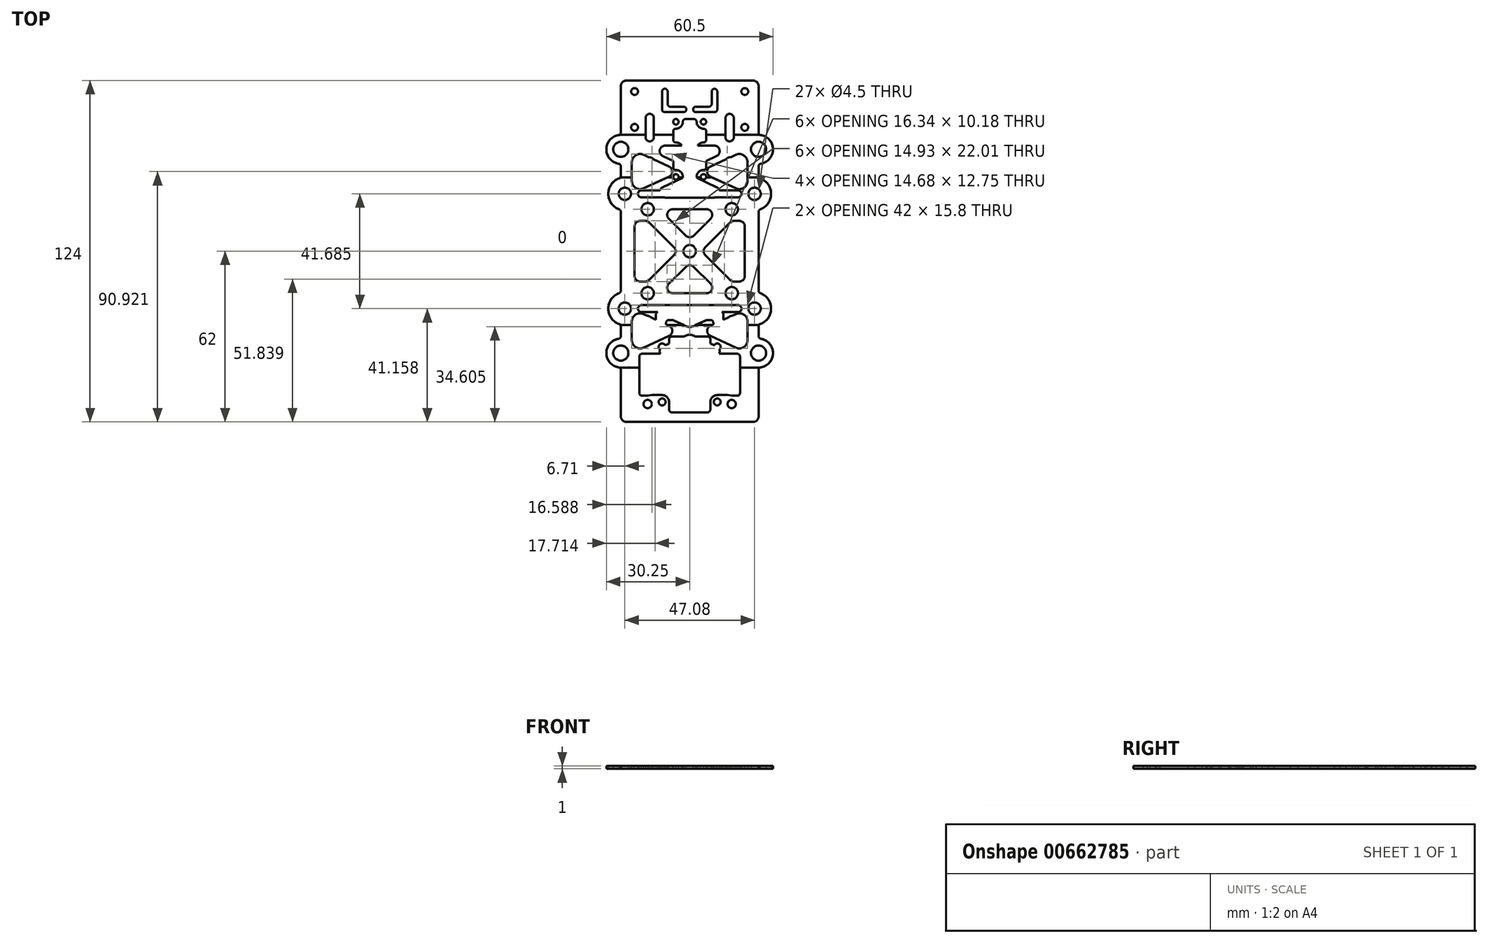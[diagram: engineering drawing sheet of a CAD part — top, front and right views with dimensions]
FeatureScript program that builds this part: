
annotation { "Feature Type Name" : "Feature", "Feature Type Description" : "" }
export const myFeature = defineFeature(function(context is Context, id is Id, definition is map)
    precondition{}
    {
        {
            var Q0;
            Q0=qCreatedBy(makeId("Top.planeOp"),FACE);
            var sketch = newSketch(context, id + "F0", { "sketchPlane" : qUnion([Q0])});
            skLineSegment(sketch, "E0.bottom", {"start": v(15.25, 15.25) * mm, "end": v(-15.25, 15.25) * mm, "construction": true});
            skLineSegment(sketch, "E0.top", {"start": v(15.25, -15.25) * mm, "end": v(-15.25, -15.25) * mm, "construction": true});
            skLineSegment(sketch, "E0.left", {"start": v(15.25, 15.25) * mm, "end": v(15.25, -15.25) * mm, "construction": true});
            skLineSegment(sketch, "E0.right", {"start": v(-15.25, 15.25) * mm, "end": v(-15.25, -15.25) * mm, "construction": true});
            skPoint(sketch, "E0.middle", {"position": v(0, 0) * mm});
            skLineSegment(sketch, "E1", {"start": v(15.25, 15.25) * mm, "end": v(23.54, 20.84) * mm});
            skLineSegment(sketch, "E2", {"start": v(23.54, 20.84) * mm, "end": v(92.7, 67.5) * mm});
            skCircle(sketch, "E3", {"center": v(92.7, 67.5) * mm, "radius": 63.5 * mm, "construction": true});
            skLineSegment(sketch, "E4", {"start": v(0, 0) * mm, "end": v(92.7, 0) * mm, "construction": true});
            skLineSegment(sketch, "E5.bottom", {"start": v(-25, 37) * mm, "end": v(25, 37) * mm, "construction": true});
            skLineSegment(sketch, "E5.top", {"start": v(-25, -37) * mm, "end": v(25, -37) * mm, "construction": true});
            skLineSegment(sketch, "E5.left", {"start": v(-25, 37) * mm, "end": v(-25, -37) * mm, "construction": true});
            skLineSegment(sketch, "E5.right", {"start": v(25, 37) * mm, "end": v(25, -37) * mm, "construction": true});
            skCircle(sketch, "E6", {"center": v(25, 37) * mm, "radius": 4.25 * mm, "construction": true});
            skCircle(sketch, "E7", {"center": v(15.25, 15.25) * mm, "radius": 1.5 * mm, "construction": true});
            skCircle(sketch, "E8", {"center": v(23.54, 20.84) * mm, "radius": 1.5 * mm, "construction": true});
            skCircle(sketch, "E9", {"center": v(92.7, 67.5) * mm, "radius": 50.8 * mm, "construction": true});
            skLineSegment(sketch, "E10.bottom", {"start": v(11.34, 21.05) * mm, "end": v(88.79, 73.3) * mm, "construction": true});
            skLineSegment(sketch, "E10.top", {"start": v(19.16, 9.45) * mm, "end": v(96.62, 61.7) * mm, "construction": true});
            skLineSegment(sketch, "E10.left", {"start": v(11.34, 21.05) * mm, "end": v(19.16, 9.45) * mm, "construction": true});
            skLineSegment(sketch, "E10.right", {"start": v(88.79, 73.3) * mm, "end": v(96.62, 61.7) * mm, "construction": true});
            skCircle(sketch, "E11", {"center": v(-25, 37) * mm, "radius": 4.25 * mm, "construction": true});
            skCircle(sketch, "E12", {"center": v(-25, -37) * mm, "radius": 4.25 * mm, "construction": true});
            skCircle(sketch, "E13", {"center": v(25, -37) * mm, "radius": 4.25 * mm, "construction": true});
            skCircle(sketch, "E14", {"center": v(-15.25, 15.25) * mm, "radius": 1.5 * mm, "construction": true});
            skCircle(sketch, "E15", {"center": v(-15.25, -15.25) * mm, "radius": 1.5 * mm, "construction": true});
            skCircle(sketch, "E16", {"center": v(15.25, -15.25) * mm, "radius": 1.5 * mm, "construction": true});
            skCircle(sketch, "E17.MirrorC", {"center": v(-23.54, 20.84) * mm, "radius": 1.5 * mm, "construction": true});
            skCircle(sketch, "E18.MirrorC", {"center": v(-23.54, -20.84) * mm, "radius": 1.5 * mm, "construction": true});
            skCircle(sketch, "E19.MirrorC", {"center": v(23.54, -20.84) * mm, "radius": 1.5 * mm, "construction": true});
            skSolve(sketch);
        }
        {
            var Q0;
            Q0=qCreatedBy(makeId("Top.planeOp"),FACE);
            var sketch = newSketch(context, id + "F1", { "sketchPlane" : qUnion([Q0])});
            skPoint(sketch, "E20.0", {"position": v(-25, 37) * mm});
            skPoint(sketch, "E21.0", {"position": v(25, 37) * mm});
            skPoint(sketch, "E22.0", {"position": v(25, -37) * mm});
            skPoint(sketch, "E23.0", {"position": v(-25, -37) * mm});
            skCircle(sketch, "E24.0", {"center": v(-23.54, -20.84) * mm, "radius": 1.5 * mm});
            skCircle(sketch, "E25.0", {"center": v(-15.25, -15.25) * mm, "radius": 1.5 * mm});
            skCircle(sketch, "E26.0", {"center": v(15.25, -15.25) * mm, "radius": 1.5 * mm});
            skCircle(sketch, "E27.0", {"center": v(23.54, -20.84) * mm, "radius": 1.5 * mm});
            skCircle(sketch, "E28.0", {"center": v(15.25, 15.25) * mm, "radius": 1.5 * mm});
            skCircle(sketch, "E29.0", {"center": v(-15.25, 15.25) * mm, "radius": 1.5 * mm});
            skCircle(sketch, "E30.0", {"center": v(-23.54, 20.84) * mm, "radius": 1.5 * mm});
            skCircle(sketch, "E31.0", {"center": v(23.54, 20.84) * mm, "radius": 1.5 * mm});
            skCircle(sketch, "E32", {"center": v(25, 37) * mm, "radius": 2.75 * mm});
            skCircle(sketch, "E33", {"center": v(-25, 37) * mm, "radius": 2.75 * mm});
            skCircle(sketch, "E34", {"center": v(-25, -37) * mm, "radius": 2.75 * mm});
            skCircle(sketch, "E35", {"center": v(25, -37) * mm, "radius": 2.75 * mm});
            skSolve(sketch);
        }
        {
            var Q0;
            Q0=qCreatedBy(makeId("Top.planeOp"),FACE);
            var sketch = newSketch(context, id + "F2", { "sketchPlane" : qUnion([Q0])});
            skCircle(sketch, "E36.0", {"center": v(-25, -37) * mm, "radius": 2.75 * mm});
            skCircle(sketch, "E37.0", {"center": v(-23.54, -20.84) * mm, "radius": 1.5 * mm});
            skCircle(sketch, "E38.0", {"center": v(-15.25, -15.25) * mm, "radius": 1.5 * mm});
            skCircle(sketch, "E39.0", {"center": v(15.25, -15.25) * mm, "radius": 1.5 * mm});
            skCircle(sketch, "E40.0", {"center": v(23.54, -20.84) * mm, "radius": 1.5 * mm});
            skCircle(sketch, "E41.0", {"center": v(-25, 37) * mm, "radius": 2.75 * mm});
            skCircle(sketch, "E42.0", {"center": v(-23.54, 20.84) * mm, "radius": 1.5 * mm});
            skCircle(sketch, "E43.0", {"center": v(-15.25, 15.25) * mm, "radius": 1.5 * mm});
            skCircle(sketch, "E44.0", {"center": v(15.25, 15.25) * mm, "radius": 1.5 * mm});
            skCircle(sketch, "E45.0", {"center": v(23.54, 20.84) * mm, "radius": 1.5 * mm});
            skCircle(sketch, "E46.0", {"center": v(25, 37) * mm, "radius": 2.75 * mm});
            skLineSegment(sketch, "E47.bottom", {"start": v(25, 62) * mm, "end": v(-25, 62) * mm});
            skLineSegment(sketch, "E47.top", {"start": v(25, -62) * mm, "end": v(-25, -62) * mm});
            skLineSegment(sketch, "E47.left", {"start": v(25, 62) * mm, "end": v(25, 42.25) * mm});
            skLineSegment(sketch, "E47.right", {"start": v(-25, 62) * mm, "end": v(-25, 42.25) * mm});
            skPoint(sketch, "E47.middle", {"position": v(0, 0) * mm});
            skArc(sketch, "E48", {"start": v(-25, 42.25) * mm, "mid": v(-30.25, 37) * mm, "end": v(-25, 31.75) * mm});
            skArc(sketch, "E49", {"start": v(-25, 26.66) * mm, "mid": v(-29.54, 20.84) * mm, "end": v(-25, 15.02) * mm});
            skArc(sketch, "E50", {"start": v(-25, -15.02) * mm, "mid": v(-29.54, -20.84) * mm, "end": v(-25, -26.66) * mm});
            skArc(sketch, "E51.MirrorCS", {"start": v(25, 42.25) * mm, "mid": v(30.25, 37) * mm, "end": v(25, 31.75) * mm});
            skArc(sketch, "E52.MirrorCS", {"start": v(25, 26.66) * mm, "mid": v(29.54, 20.84) * mm, "end": v(25, 15.02) * mm});
            skArc(sketch, "E53.MirrorCS", {"start": v(25, -15.02) * mm, "mid": v(29.54, -20.84) * mm, "end": v(25, -26.66) * mm});
            skArc(sketch, "E54", {"start": v(-25, -31.75) * mm, "mid": v(-30.25, -37) * mm, "end": v(-25, -42.25) * mm});
            skArc(sketch, "E55.MirrorCS", {"start": v(25, -31.75) * mm, "mid": v(30.25, -37) * mm, "end": v(25, -42.25) * mm});
            skLineSegment(sketch, "E56", {"start": v(-25, 42.25) * mm, "end": v(-25, 39.75) * mm, "construction": true});
            skLineSegment(sketch, "E57", {"start": v(-25, 31.75) * mm, "end": v(-25, 26.66) * mm});
            skLineSegment(sketch, "E58", {"start": v(-25, 34.25) * mm, "end": v(-25, 31.75) * mm, "construction": true});
            skLineSegment(sketch, "E59", {"start": v(-25, 39.75) * mm, "end": v(-25, 34.25) * mm, "construction": true});
            skLineSegment(sketch, "E60", {"start": v(25, 39.75) * mm, "end": v(25, 34.25) * mm, "construction": true});
            skLineSegment(sketch, "E61", {"start": v(25, 42.25) * mm, "end": v(25, 39.75) * mm, "construction": true});
            skLineSegment(sketch, "E62", {"start": v(25, 34.25) * mm, "end": v(25, 31.75) * mm, "construction": true});
            skLineSegment(sketch, "E63", {"start": v(25, 31.75) * mm, "end": v(25, 26.66) * mm});
            skLineSegment(sketch, "E64", {"start": v(-25, 26.66) * mm, "end": v(-25, 15.02) * mm, "construction": true});
            skLineSegment(sketch, "E65", {"start": v(-25, 15.02) * mm, "end": v(-25, -15.02) * mm});
            skLineSegment(sketch, "E66", {"start": v(25, 26.66) * mm, "end": v(25, 15.02) * mm, "construction": true});
            skLineSegment(sketch, "E67", {"start": v(25, 15.02) * mm, "end": v(25, -15.02) * mm});
            skLineSegment(sketch, "E68", {"start": v(-25, -31.75) * mm, "end": v(-25, -34.25) * mm, "construction": true});
            skLineSegment(sketch, "E69", {"start": v(-25, -42.25) * mm, "end": v(-25, -62) * mm});
            skLineSegment(sketch, "E70", {"start": v(-25, -39.75) * mm, "end": v(-25, -42.25) * mm, "construction": true});
            skLineSegment(sketch, "E71", {"start": v(-25, -34.25) * mm, "end": v(-25, -39.75) * mm, "construction": true});
            skLineSegment(sketch, "E72", {"start": v(-25, -26.66) * mm, "end": v(-25, -31.75) * mm});
            skLineSegment(sketch, "E73", {"start": v(-25, -15.02) * mm, "end": v(-25, -26.66) * mm, "construction": true});
            skLineSegment(sketch, "E74", {"start": v(25, -15.02) * mm, "end": v(25, -26.66) * mm});
            skLineSegment(sketch, "E75", {"start": v(25, -26.66) * mm, "end": v(25, -31.75) * mm});
            skLineSegment(sketch, "E76", {"start": v(25, -31.75) * mm, "end": v(25, -42.25) * mm, "construction": true});
            skLineSegment(sketch, "E77", {"start": v(25, -42.25) * mm, "end": v(25, -42.25) * mm});
            skArc(sketch, "E78", {"start": v(25, -34.25) * mm, "mid": v(22.25, -37) * mm, "end": v(25, -39.75) * mm});
            skArc(sketch, "E79", {"start": v(25, -39.75) * mm, "mid": v(27.75, -37) * mm, "end": v(25, -34.25) * mm});
            skLineSegment(sketch, "E80", {"start": v(25, -42.25) * mm, "end": v(25, -62) * mm});
            skSolve(sketch);
        }
        {
            var Q0;
            Q0=qSketchRegion(id+"F2",true);
            extrude(context, id + "F3", {"entities" : qUnion([Q0]), "depth" : 1 * mm, "offsetDistance" : 25 * mm});
        }
        {
            var Q0;
            Q0=qCreatedBy(makeId("Top.planeOp"),FACE);
            var sketch = newSketch(context, id + "F4", { "sketchPlane" : qUnion([Q0])});
            skCircle(sketch, "E81.0", {"center": v(-23.54, 20.84) * mm, "radius": 1.5 * mm});
            skCircle(sketch, "E82.0", {"center": v(-15.25, 15.25) * mm, "radius": 1.5 * mm});
            skCircle(sketch, "E83.0", {"center": v(15.25, 15.25) * mm, "radius": 1.5 * mm});
            skCircle(sketch, "E84.0", {"center": v(23.54, 20.84) * mm, "radius": 1.5 * mm});
            skCircle(sketch, "E85.0", {"center": v(-15.25, -15.25) * mm, "radius": 1.5 * mm});
            skCircle(sketch, "E86.0", {"center": v(-23.54, -20.84) * mm, "radius": 1.5 * mm});
            skCircle(sketch, "E87.0", {"center": v(15.25, -15.25) * mm, "radius": 1.5 * mm});
            skCircle(sketch, "E88.0", {"center": v(23.54, -20.84) * mm, "radius": 1.5 * mm});
            skArc(sketch, "E89.0", {"start": v(-25, 26.66) * mm, "mid": v(-29.54, 20.84) * mm, "end": v(-25, 15.02) * mm});
            skLineSegment(sketch, "E90.0", {"start": v(-25, 15.02) * mm, "end": v(-25, -15.02) * mm});
            skArc(sketch, "E91.0", {"start": v(-25, -15.02) * mm, "mid": v(-29.54, -20.84) * mm, "end": v(-25, -26.66) * mm});
            skLineSegment(sketch, "E92.0", {"start": v(25, 15.02) * mm, "end": v(25, -15.02) * mm});
            skArc(sketch, "E93.0", {"start": v(25, 26.66) * mm, "mid": v(29.54, 20.84) * mm, "end": v(25, 15.02) * mm});
            skArc(sketch, "E94.0", {"start": v(25, -15.02) * mm, "mid": v(29.54, -20.84) * mm, "end": v(25, -26.66) * mm});
            skArc(sketch, "E95", {"start": v(-25, 26.66) * mm, "mid": v(-24.28, 26.8) * mm, "end": v(-23.54, 26.84) * mm});
            skArc(sketch, "E96", {"start": v(-25, -26.66) * mm, "mid": v(-24.28, -26.8) * mm, "end": v(-23.54, -26.84) * mm});
            skArc(sketch, "E97", {"start": v(25, 26.66) * mm, "mid": v(24.28, 26.8) * mm, "end": v(23.54, 26.84) * mm});
            skArc(sketch, "E98", {"start": v(25, -26.66) * mm, "mid": v(24.28, -26.8) * mm, "end": v(23.54, -26.84) * mm});
            skLineSegment(sketch, "E99", {"start": v(-23.54, 26.84) * mm, "end": v(23.54, 26.84) * mm});
            skLineSegment(sketch, "E100", {"start": v(-23.54, -26.84) * mm, "end": v(23.54, -26.84) * mm});
            skSolve(sketch);
        }
        {
            var Q0;
            Q0=qCreatedBy(makeId("Top.planeOp"),FACE);
            var sketch = newSketch(context, id + "F5", { "sketchPlane" : qUnion([Q0])});
            skArc(sketch, "E101.0.0", {"start": v(25, -26.66) * mm, "mid": v(29.54, -20.84) * mm, "end": v(25, -15.02) * mm});
            skLineSegment(sketch, "E101.0.1", {"start": v(25, -15.02) * mm, "end": v(25, 15.02) * mm});
            skArc(sketch, "E101.0.2", {"start": v(25, 15.02) * mm, "mid": v(29.54, 20.84) * mm, "end": v(25, 26.66) * mm});
            skLineSegment(sketch, "E101.0.3", {"start": v(25, 26.66) * mm, "end": v(25, 31.75) * mm});
            skArc(sketch, "E101.0.4", {"start": v(25, 31.75) * mm, "mid": v(30.25, 37) * mm, "end": v(25, 42.25) * mm});
            skLineSegment(sketch, "E101.0.5", {"start": v(25, 42.25) * mm, "end": v(25, 62) * mm});
            skLineSegment(sketch, "E101.0.6", {"start": v(25, 62) * mm, "end": v(-25, 62) * mm, "construction": true});
            skLineSegment(sketch, "E101.0.7", {"start": v(-25, 62) * mm, "end": v(-25, 42.25) * mm});
            skArc(sketch, "E101.0.8", {"start": v(-25, 42.25) * mm, "mid": v(-30.25, 37) * mm, "end": v(-25, 31.75) * mm});
            skLineSegment(sketch, "E101.0.9", {"start": v(-25, 31.75) * mm, "end": v(-25, 26.66) * mm});
            skArc(sketch, "E101.0.10", {"start": v(-25, 26.66) * mm, "mid": v(-29.54, 20.84) * mm, "end": v(-25, 15.02) * mm});
            skLineSegment(sketch, "E101.0.11", {"start": v(-25, 15.02) * mm, "end": v(-25, -15.02) * mm});
            skArc(sketch, "E101.0.12", {"start": v(-25, -15.02) * mm, "mid": v(-29.54, -20.84) * mm, "end": v(-25, -26.66) * mm});
            skLineSegment(sketch, "E101.0.13", {"start": v(-25, -26.66) * mm, "end": v(-25, -31.75) * mm});
            skArc(sketch, "E101.0.14", {"start": v(-25, -31.75) * mm, "mid": v(-30.25, -37) * mm, "end": v(-25, -42.25) * mm});
            skLineSegment(sketch, "E101.0.15", {"start": v(-25, -42.25) * mm, "end": v(-25, -62) * mm});
            skLineSegment(sketch, "E101.0.16", {"start": v(-25, -62) * mm, "end": v(25, -62) * mm, "construction": true});
            skLineSegment(sketch, "E101.0.17", {"start": v(25, -62) * mm, "end": v(25, -42.25) * mm});
            skArc(sketch, "E101.0.18", {"start": v(25, -42.25) * mm, "mid": v(30.25, -37) * mm, "end": v(25, -31.75) * mm});
            skLineSegment(sketch, "E101.0.19", {"start": v(25, -31.75) * mm, "end": v(25, -26.66) * mm});
            skLineSegment(sketch, "E102", {"start": v(-25, 42.25) * mm, "end": v(25, 42.25) * mm});
            skLineSegment(sketch, "E103", {"start": v(-25, -42.25) * mm, "end": v(25, -42.25) * mm});
            skCircle(sketch, "E104.0", {"center": v(-25, 37) * mm, "radius": 2.75 * mm});
            skCircle(sketch, "E105.0", {"center": v(-23.54, 20.84) * mm, "radius": 1.5 * mm});
            skCircle(sketch, "E106.0", {"center": v(-15.25, 15.25) * mm, "radius": 1.5 * mm});
            skCircle(sketch, "E107.0", {"center": v(15.25, 15.25) * mm, "radius": 1.5 * mm});
            skCircle(sketch, "E108.0", {"center": v(23.54, 20.84) * mm, "radius": 1.5 * mm});
            skCircle(sketch, "E109.0", {"center": v(25, 37) * mm, "radius": 2.75 * mm});
            skCircle(sketch, "E110.0", {"center": v(-23.54, -20.84) * mm, "radius": 1.5 * mm});
            skCircle(sketch, "E111.0", {"center": v(-15.25, -15.25) * mm, "radius": 1.5 * mm});
            skCircle(sketch, "E112.0", {"center": v(15.25, -15.25) * mm, "radius": 1.5 * mm});
            skCircle(sketch, "E113.0", {"center": v(23.54, -20.84) * mm, "radius": 1.5 * mm});
            skCircle(sketch, "E114.0", {"center": v(-25, -37) * mm, "radius": 2.75 * mm});
            skCircle(sketch, "E115.0", {"center": v(25, -37) * mm, "radius": 2.75 * mm});
            skSolve(sketch);
        }
        {
            var Q0;
            Q0=qSketchRegion(id+"F4",true);
            extrude(context, id + "F6", {"entities" : qUnion([Q0]), "depth" : 1 * mm, "offsetDistance" : 25 * mm});
        }
        {
            var Q0;
            Q0=qSketchRegion(id+"F5",true);
            extrude(context, id + "F7", {"entities" : qUnion([Q0]), "depth" : 1 * mm, "offsetDistance" : 25 * mm});
        }
        {
            var Q0;
            Q0=makeQuery(id+"F3.opExtrude","SWEPT_EDGE",EDGE,{"disambiguationData":[OSD([sQuery(id+"F2.wireOp",EDGE,"E47.top"),sQuery(id+"F2.wireOp",EDGE,"E69")])]});
            var Q1;
            Q1=makeQuery(id+"F3.opExtrude","SWEPT_EDGE",EDGE,{"disambiguationData":[OSD([sQuery(id+"F2.wireOp",EDGE,"E47.top"),sQuery(id+"F2.wireOp",EDGE,"E80")])]});
            var Q2;
            Q2=makeQuery(id+"F3.opExtrude","SWEPT_EDGE",EDGE,{"disambiguationData":[OSD([sQuery(id+"F2.wireOp",EDGE,"E47.bottom"),sQuery(id+"F2.wireOp",EDGE,"E47.right")])]});
            var Q3;
            Q3=makeQuery(id+"F3.opExtrude","SWEPT_EDGE",EDGE,{"disambiguationData":[OSD([sQuery(id+"F2.wireOp",EDGE,"E47.bottom"),sQuery(id+"F2.wireOp",EDGE,"E47.left")])]});
            fillet(context, id + "F8", {"entities" : qUnion([Q0, Q1, Q2, Q3]), "radius" : 2 * mm, "allowEdgeOverflow" : false});
        }
        {
            var Q0;
            Q0=makeQuery(id+"F3.opExtrude","SWEPT_EDGE",EDGE,{"disambiguationData":[OSD([sQuery(id+"F2.wireOp",EDGE,"E47.left"),sQuery(id+"F2.wireOp",EDGE,"E51.MirrorCS")])]});
            var Q1;
            Q1=makeQuery(id+"F3.opExtrude","SWEPT_EDGE",EDGE,{"disambiguationData":[OSD([sQuery(id+"F2.wireOp",EDGE,"E51.MirrorCS"),sQuery(id+"F2.wireOp",EDGE,"E63")])]});
            var Q2;
            Q2=makeQuery(id+"F3.opExtrude","SWEPT_EDGE",EDGE,{"disambiguationData":[OSD([sQuery(id+"F2.wireOp",EDGE,"E52.MirrorCS"),sQuery(id+"F2.wireOp",EDGE,"E63")])]});
            var Q3;
            Q3=makeQuery(id+"F3.opExtrude","SWEPT_EDGE",EDGE,{"disambiguationData":[OSD([sQuery(id+"F2.wireOp",EDGE,"E52.MirrorCS"),sQuery(id+"F2.wireOp",EDGE,"E67")])]});
            var Q4;
            Q4=makeQuery(id+"F3.opExtrude","SWEPT_EDGE",EDGE,{"disambiguationData":[OSD([sQuery(id+"F2.wireOp",EDGE,"E53.MirrorCS"),sQuery(id+"F2.wireOp",EDGE,"E67"),sQuery(id+"F2.wireOp",EDGE,"E74")])]});
            var Q5;
            Q5=makeQuery(id+"F3.opExtrude","SWEPT_EDGE",EDGE,{"disambiguationData":[OSD([sQuery(id+"F2.wireOp",EDGE,"E55.MirrorCS"),sQuery(id+"F2.wireOp",EDGE,"E75")])]});
            var Q6;
            Q6=makeQuery(id+"F3.opExtrude","SWEPT_EDGE",EDGE,{"disambiguationData":[OSD([sQuery(id+"F2.wireOp",EDGE,"E55.MirrorCS"),sQuery(id+"F2.wireOp",EDGE,"E80")])]});
            var Q7;
            Q7=makeQuery(id+"F3.opExtrude","SWEPT_EDGE",EDGE,{"disambiguationData":[OSD([sQuery(id+"F2.wireOp",EDGE,"E47.right"),sQuery(id+"F2.wireOp",EDGE,"E48")])]});
            var Q8;
            Q8=makeQuery(id+"F3.opExtrude","SWEPT_EDGE",EDGE,{"disambiguationData":[OSD([sQuery(id+"F2.wireOp",EDGE,"E49"),sQuery(id+"F2.wireOp",EDGE,"E57")])]});
            var Q9;
            Q9=makeQuery(id+"F3.opExtrude","SWEPT_EDGE",EDGE,{"disambiguationData":[OSD([sQuery(id+"F2.wireOp",EDGE,"E48"),sQuery(id+"F2.wireOp",EDGE,"E57")])]});
            var Q10;
            Q10=makeQuery(id+"F3.opExtrude","SWEPT_EDGE",EDGE,{"disambiguationData":[OSD([sQuery(id+"F2.wireOp",EDGE,"E49"),sQuery(id+"F2.wireOp",EDGE,"E65")])]});
            var Q11;
            Q11=makeQuery(id+"F3.opExtrude","SWEPT_EDGE",EDGE,{"disambiguationData":[OSD([sQuery(id+"F2.wireOp",EDGE,"E50"),sQuery(id+"F2.wireOp",EDGE,"E72")])]});
            var Q12;
            Q12=makeQuery(id+"F3.opExtrude","SWEPT_EDGE",EDGE,{"disambiguationData":[OSD([sQuery(id+"F2.wireOp",EDGE,"E50"),sQuery(id+"F2.wireOp",EDGE,"E65")])]});
            var Q13;
            Q13=makeQuery(id+"F3.opExtrude","SWEPT_EDGE",EDGE,{"disambiguationData":[OSD([sQuery(id+"F2.wireOp",EDGE,"E54"),sQuery(id+"F2.wireOp",EDGE,"E72")])]});
            var Q14;
            Q14=makeQuery(id+"F3.opExtrude","SWEPT_EDGE",EDGE,{"disambiguationData":[OSD([sQuery(id+"F2.wireOp",EDGE,"E54"),sQuery(id+"F2.wireOp",EDGE,"E69")])]});
            var Q15;
            Q15=makeQuery(id+"F7.opExtrude","SWEPT_EDGE",EDGE,{"disambiguationData":[OSD([sQuery(id+"F5.wireOp",EDGE,"E101.0.9"),sQuery(id+"F5.wireOp",EDGE,"E101.0.10")])]});
            var Q16;
            Q16=makeQuery(id+"F7.opExtrude","SWEPT_EDGE",EDGE,{"disambiguationData":[OSD([sQuery(id+"F5.wireOp",EDGE,"E101.0.8"),sQuery(id+"F5.wireOp",EDGE,"E101.0.9")])]});
            var Q17;
            Q17=makeQuery(id+"F7.opExtrude","SWEPT_EDGE",EDGE,{"disambiguationData":[OSD([sQuery(id+"F5.wireOp",EDGE,"E101.0.10"),sQuery(id+"F5.wireOp",EDGE,"E101.0.11")])]});
            var Q18;
            Q18=makeQuery(id+"F7.opExtrude","SWEPT_EDGE",EDGE,{"disambiguationData":[OSD([sQuery(id+"F5.wireOp",EDGE,"E101.0.11"),sQuery(id+"F5.wireOp",EDGE,"E101.0.12")])]});
            var Q19;
            Q19=makeQuery(id+"F7.opExtrude","SWEPT_EDGE",EDGE,{"disambiguationData":[OSD([sQuery(id+"F5.wireOp",EDGE,"E101.0.12"),sQuery(id+"F5.wireOp",EDGE,"E101.0.13")])]});
            var Q20;
            Q20=makeQuery(id+"F7.opExtrude","SWEPT_EDGE",EDGE,{"disambiguationData":[OSD([sQuery(id+"F5.wireOp",EDGE,"E101.0.13"),sQuery(id+"F5.wireOp",EDGE,"E101.0.14")])]});
            var Q21;
            Q21=makeQuery(id+"F7.opExtrude","SWEPT_EDGE",EDGE,{"disambiguationData":[OSD([sQuery(id+"F5.wireOp",EDGE,"E101.0.1"),sQuery(id+"F5.wireOp",EDGE,"E101.0.2")])]});
            var Q22;
            Q22=makeQuery(id+"F7.opExtrude","SWEPT_EDGE",EDGE,{"disambiguationData":[OSD([sQuery(id+"F5.wireOp",EDGE,"E101.0.2"),sQuery(id+"F5.wireOp",EDGE,"E101.0.3")])]});
            var Q23;
            Q23=makeQuery(id+"F7.opExtrude","SWEPT_EDGE",EDGE,{"disambiguationData":[OSD([sQuery(id+"F5.wireOp",EDGE,"E101.0.3"),sQuery(id+"F5.wireOp",EDGE,"E101.0.4")])]});
            var Q24;
            Q24=makeQuery(id+"F7.opExtrude","SWEPT_EDGE",EDGE,{"disambiguationData":[OSD([sQuery(id+"F5.wireOp",EDGE,"E101.0.18"),sQuery(id+"F5.wireOp",EDGE,"E101.0.19")])]});
            var Q25;
            Q25=makeQuery(id+"F7.opExtrude","SWEPT_EDGE",EDGE,{"disambiguationData":[OSD([sQuery(id+"F5.wireOp",EDGE,"E101.0.0"),sQuery(id+"F5.wireOp",EDGE,"E101.0.19")])]});
            var Q26;
            Q26=makeQuery(id+"F7.opExtrude","SWEPT_EDGE",EDGE,{"disambiguationData":[OSD([sQuery(id+"F5.wireOp",EDGE,"E101.0.0"),sQuery(id+"F5.wireOp",EDGE,"E101.0.1")])]});
            var Q27;
            Q27=makeQuery(id+"F3.opExtrude","SWEPT_EDGE",EDGE,{"disambiguationData":[OSD([sQuery(id+"F2.wireOp",EDGE,"E53.MirrorCS"),sQuery(id+"F2.wireOp",EDGE,"E74"),sQuery(id+"F2.wireOp",EDGE,"E75")])]});
            var Q28;
            Q28=makeQuery(id+"F6.opExtrude","SWEPT_EDGE",EDGE,{"disambiguationData":[OSD([sQuery(id+"F4.wireOp",EDGE,"E92.0"),sQuery(id+"F4.wireOp",EDGE,"E94.0")])]});
            var Q29;
            Q29=makeQuery(id+"F6.opExtrude","SWEPT_EDGE",EDGE,{"disambiguationData":[OSD([sQuery(id+"F4.wireOp",EDGE,"E92.0"),sQuery(id+"F4.wireOp",EDGE,"E93.0")])]});
            var Q30;
            Q30=makeQuery(id+"F6.opExtrude","SWEPT_EDGE",EDGE,{"disambiguationData":[OSD([sQuery(id+"F4.wireOp",EDGE,"E89.0"),sQuery(id+"F4.wireOp",EDGE,"E90.0")])]});
            var Q31;
            Q31=makeQuery(id+"F6.opExtrude","SWEPT_EDGE",EDGE,{"disambiguationData":[OSD([sQuery(id+"F4.wireOp",EDGE,"E90.0"),sQuery(id+"F4.wireOp",EDGE,"E91.0")])]});
            fillet(context, id + "F9", {"entities" : qUnion([Q0, Q1, Q2, Q3, Q4, Q5, Q6, Q7, Q8, Q9, Q10, Q11, Q12, Q13, Q14, Q15, Q16, Q17, Q18, Q19, Q20, Q21, Q22, Q23, Q24, Q25, Q26, Q27, Q28, Q29, Q30, Q31]), "radius" : 1 * mm, "allowEdgeOverflow" : false});
        }
        {
            var Q0;
            Q0=makeQuery(id+"F3.opExtrude","CAP_FACE",FACE,{"disambiguationData":[OSD([sQuery(id+"F2.wireOp",EDGE,"E36.0"),sQuery(id+"F2.wireOp",EDGE,"E37.0"),sQuery(id+"F2.wireOp",EDGE,"E38.0"),sQuery(id+"F2.wireOp",EDGE,"E39.0"),sQuery(id+"F2.wireOp",EDGE,"E40.0"),sQuery(id+"F2.wireOp",EDGE,"E41.0"),sQuery(id+"F2.wireOp",EDGE,"E42.0"),sQuery(id+"F2.wireOp",EDGE,"E43.0"),sQuery(id+"F2.wireOp",EDGE,"E44.0"),sQuery(id+"F2.wireOp",EDGE,"E45.0"),sQuery(id+"F2.wireOp",EDGE,"E46.0"),sQuery(id+"F2.wireOp",EDGE,"E47.bottom"),sQuery(id+"F2.wireOp",EDGE,"E47.top"),sQuery(id+"F2.wireOp",EDGE,"E47.left"),sQuery(id+"F2.wireOp",EDGE,"E47.right"),sQuery(id+"F2.wireOp",EDGE,"E48"),sQuery(id+"F2.wireOp",EDGE,"E49"),sQuery(id+"F2.wireOp",EDGE,"E50"),sQuery(id+"F2.wireOp",EDGE,"E51.MirrorCS"),sQuery(id+"F2.wireOp",EDGE,"E52.MirrorCS"),sQuery(id+"F2.wireOp",EDGE,"E53.MirrorCS"),sQuery(id+"F2.wireOp",EDGE,"E54"),sQuery(id+"F2.wireOp",EDGE,"E55.MirrorCS"),sQuery(id+"F2.wireOp",EDGE,"rjWOpLop-ofpK-hTEo-auwK-LkPdoEbubAMj"),sQuery(id+"F2.wireOp",EDGE,"E57"),sQuery(id+"F2.wireOp",EDGE,"E63"),sQuery(id+"F2.wireOp",EDGE,"E65"),sQuery(id+"F2.wireOp",EDGE,"E67"),sQuery(id+"F2.wireOp",EDGE,"E69"),sQuery(id+"F2.wireOp",EDGE,"E72"),sQuery(id+"F2.wireOp",EDGE,"E75"),sQuery(id+"F2.wireOp",EDGE,"E78"),sQuery(id+"F2.wireOp",EDGE,"E79"),sQuery(id+"F2.wireOp",EDGE,"E80")])],"isStart":false});
            var sketch = newSketch(context, id + "F10", { "sketchPlane" : qUnion([Q0])});
            skLineSegment(sketch, "E116.0.0", {"start": v(25, 43.17) * mm, "end": v(25, 60) * mm, "construction": true});
            skArc(sketch, "E116.0.1", {"start": v(25, 60) * mm, "mid": v(24.41, 61.41) * mm, "end": v(23, 62) * mm, "construction": true});
            skLineSegment(sketch, "E116.0.2", {"start": v(23, 62) * mm, "end": v(-23, 62) * mm, "construction": true});
            skArc(sketch, "E116.0.3", {"start": v(-23, 62) * mm, "mid": v(-24.41, 61.41) * mm, "end": v(-25, 60) * mm, "construction": true});
            skLineSegment(sketch, "E116.0.4", {"start": v(-25, 60) * mm, "end": v(-25, 43.17) * mm, "construction": true});
            skArc(sketch, "E116.0.5", {"start": v(-25, 43.17) * mm, "mid": v(-25.24, 42.52) * mm, "end": v(-25.84, 42.18) * mm, "construction": true});
            skArc(sketch, "E116.0.6", {"start": v(-25.84, 42.18) * mm, "mid": v(-30.25, 37) * mm, "end": v(-25.84, 31.82) * mm, "construction": true});
            skArc(sketch, "E116.0.7", {"start": v(-25.84, 31.82) * mm, "mid": v(-25.24, 31.48) * mm, "end": v(-25, 30.83) * mm, "construction": true});
            skLineSegment(sketch, "E116.0.8", {"start": v(-25, 30.83) * mm, "end": v(-25, 27.4) * mm, "construction": true});
            skArc(sketch, "E116.0.9", {"start": v(-25, 27.4) * mm, "mid": v(-25.18, 26.83) * mm, "end": v(-25.65, 26.46) * mm, "construction": true});
            skArc(sketch, "E116.0.10", {"start": v(-25.65, 26.46) * mm, "mid": v(-29.54, 20.84) * mm, "end": v(-25.65, 15.23) * mm, "construction": true});
            skArc(sketch, "E116.0.11", {"start": v(-25.65, 15.23) * mm, "mid": v(-25.18, 14.86) * mm, "end": v(-25, 14.29) * mm, "construction": true});
            skLineSegment(sketch, "E116.0.12", {"start": v(-25, 14.29) * mm, "end": v(-25, -14.29) * mm, "construction": true});
            skArc(sketch, "E116.0.13", {"start": v(-25, -14.29) * mm, "mid": v(-25.18, -14.86) * mm, "end": v(-25.65, -15.23) * mm, "construction": true});
            skArc(sketch, "E116.0.14", {"start": v(-25.65, -15.23) * mm, "mid": v(-29.54, -20.84) * mm, "end": v(-25.65, -26.46) * mm, "construction": true});
            skArc(sketch, "E116.0.15", {"start": v(-25.65, -26.46) * mm, "mid": v(-25.18, -26.83) * mm, "end": v(-25, -27.4) * mm, "construction": true});
            skLineSegment(sketch, "E116.0.16", {"start": v(-25, -27.4) * mm, "end": v(-25, -30.83) * mm, "construction": true});
            skArc(sketch, "E116.0.17", {"start": v(-25, -30.83) * mm, "mid": v(-25.24, -31.48) * mm, "end": v(-25.84, -31.82) * mm, "construction": true});
            skArc(sketch, "E116.0.18", {"start": v(-25.84, -31.82) * mm, "mid": v(-30.25, -37) * mm, "end": v(-25.84, -42.18) * mm, "construction": true});
            skArc(sketch, "E116.0.19", {"start": v(-25.84, -42.18) * mm, "mid": v(-25.24, -42.52) * mm, "end": v(-25, -43.17) * mm, "construction": true});
            skLineSegment(sketch, "E116.0.20", {"start": v(-25, -43.17) * mm, "end": v(-25, -60) * mm, "construction": true});
            skArc(sketch, "E116.0.21", {"start": v(-25, -60) * mm, "mid": v(-24.41, -61.41) * mm, "end": v(-23, -62) * mm, "construction": true});
            skLineSegment(sketch, "E116.0.22", {"start": v(-23, -62) * mm, "end": v(23, -62) * mm, "construction": true});
            skArc(sketch, "E116.0.23", {"start": v(23, -62) * mm, "mid": v(24.41, -61.41) * mm, "end": v(25, -60) * mm, "construction": true});
            skLineSegment(sketch, "E116.0.24", {"start": v(25, -60) * mm, "end": v(25, -43.17) * mm, "construction": true});
            skArc(sketch, "E116.0.25", {"start": v(25, -43.17) * mm, "mid": v(25.24, -42.52) * mm, "end": v(25.84, -42.18) * mm, "construction": true});
            skArc(sketch, "E116.0.26", {"start": v(25.84, -42.18) * mm, "mid": v(30.25, -37) * mm, "end": v(25.84, -31.82) * mm, "construction": true});
            skArc(sketch, "E116.0.27", {"start": v(25.84, -31.82) * mm, "mid": v(25.24, -31.48) * mm, "end": v(25, -30.83) * mm, "construction": true});
            skLineSegment(sketch, "E116.0.28", {"start": v(25, -30.83) * mm, "end": v(25, -27.4) * mm, "construction": true});
            skArc(sketch, "E116.0.29", {"start": v(25, -27.4) * mm, "mid": v(25.18, -26.83) * mm, "end": v(25.65, -26.46) * mm, "construction": true});
            skArc(sketch, "E116.0.30", {"start": v(25.65, -26.46) * mm, "mid": v(29.54, -20.84) * mm, "end": v(25.65, -15.23) * mm, "construction": true});
            skArc(sketch, "E116.0.31", {"start": v(25.65, -15.23) * mm, "mid": v(25.18, -14.86) * mm, "end": v(25, -14.29) * mm, "construction": true});
            skLineSegment(sketch, "E116.0.32", {"start": v(25, -14.29) * mm, "end": v(25, 14.29) * mm, "construction": true});
            skArc(sketch, "E116.0.33", {"start": v(25, 14.29) * mm, "mid": v(25.18, 14.86) * mm, "end": v(25.65, 15.23) * mm, "construction": true});
            skArc(sketch, "E116.0.34", {"start": v(25.65, 15.23) * mm, "mid": v(29.54, 20.84) * mm, "end": v(25.65, 26.46) * mm, "construction": true});
            skArc(sketch, "E116.0.35", {"start": v(25.65, 26.46) * mm, "mid": v(25.18, 26.83) * mm, "end": v(25, 27.4) * mm, "construction": true});
            skLineSegment(sketch, "E116.0.36", {"start": v(25, 27.4) * mm, "end": v(25, 30.83) * mm, "construction": true});
            skArc(sketch, "E116.0.37", {"start": v(25, 30.83) * mm, "mid": v(25.24, 31.48) * mm, "end": v(25.84, 31.82) * mm, "construction": true});
            skArc(sketch, "E116.0.38", {"start": v(25.84, 31.82) * mm, "mid": v(30.25, 37) * mm, "end": v(25.84, 42.18) * mm, "construction": true});
            skArc(sketch, "E116.0.39", {"start": v(25.84, 42.18) * mm, "mid": v(25.24, 42.52) * mm, "end": v(25, 43.17) * mm, "construction": true});
            skCircle(sketch, "E117", {"center": v(-23.54, -20.84) * mm, "radius": 2.25 * mm});
            skCircle(sketch, "E118", {"center": v(-15.25, -15.25) * mm, "radius": 2.25 * mm});
            skCircle(sketch, "E119", {"center": v(15.25, -15.25) * mm, "radius": 2.25 * mm});
            skCircle(sketch, "E120", {"center": v(23.54, -20.84) * mm, "radius": 2.25 * mm});
            skCircle(sketch, "E121", {"center": v(-15.25, 15.25) * mm, "radius": 2.25 * mm});
            skCircle(sketch, "E122", {"center": v(-23.54, 20.84) * mm, "radius": 2.25 * mm});
            skCircle(sketch, "E123", {"center": v(15.25, 15.25) * mm, "radius": 2.25 * mm});
            skCircle(sketch, "E124", {"center": v(23.54, 20.84) * mm, "radius": 2.25 * mm});
            skLineSegment(sketch, "E125.bottom", {"start": v(10, -34.75) * mm, "end": v(-10, -34.75) * mm, "construction": true});
            skLineSegment(sketch, "E125.top", {"start": v(10, -54.75) * mm, "end": v(-10, -54.75) * mm, "construction": true});
            skLineSegment(sketch, "E125.left", {"start": v(10, -34.75) * mm, "end": v(10, -54.75) * mm, "construction": true});
            skLineSegment(sketch, "E125.right", {"start": v(-10, -34.75) * mm, "end": v(-10, -54.75) * mm, "construction": true});
            skPoint(sketch, "E125.middle", {"position": v(0, -44.75) * mm});
            skCircle(sketch, "E126", {"center": v(-10, -34.75) * mm, "radius": 1.25 * mm});
            skCircle(sketch, "E127", {"center": v(10, -34.75) * mm, "radius": 1.25 * mm});
            skCircle(sketch, "E128", {"center": v(10, -54.75) * mm, "radius": 1.25 * mm});
            skCircle(sketch, "E129", {"center": v(-10, -54.75) * mm, "radius": 1.25 * mm});
            skLineSegment(sketch, "E130.bottom", {"start": v(15.25, -25) * mm, "end": v(-15.25, -25) * mm, "construction": true});
            skLineSegment(sketch, "E130.top", {"start": v(15.25, -55.5) * mm, "end": v(-15.25, -55.5) * mm, "construction": true});
            skLineSegment(sketch, "E130.left", {"start": v(15.25, -25) * mm, "end": v(15.25, -55.5) * mm, "construction": true});
            skLineSegment(sketch, "E130.right", {"start": v(-15.25, -25) * mm, "end": v(-15.25, -55.5) * mm, "construction": true});
            skPoint(sketch, "E130.middle", {"position": v(0, -40.25) * mm});
            skCircle(sketch, "E131", {"center": v(15.25, -25) * mm, "radius": 1.5 * mm});
            skCircle(sketch, "E132", {"center": v(-15.25, -25) * mm, "radius": 1.5 * mm});
            skCircle(sketch, "E133", {"center": v(-15.25, -55.5) * mm, "radius": 1.5 * mm});
            skCircle(sketch, "E134", {"center": v(15.25, -55.5) * mm, "radius": 1.5 * mm});
            skLineSegment(sketch, "E135.bottom", {"start": v(18, -22.25) * mm, "end": v(-18, -22.25) * mm, "construction": true});
            skLineSegment(sketch, "E135.top", {"start": v(18, -58.25) * mm, "end": v(-18, -58.25) * mm, "construction": true});
            skLineSegment(sketch, "E135.left", {"start": v(18, -22.25) * mm, "end": v(18, -58.25) * mm, "construction": true});
            skLineSegment(sketch, "E135.right", {"start": v(-18, -22.25) * mm, "end": v(-18, -58.25) * mm, "construction": true});
            skLineSegment(sketch, "E136.bottom", {"start": v(13.5, -31.25) * mm, "end": v(-13.5, -31.25) * mm, "construction": true});
            skLineSegment(sketch, "E136.top", {"start": v(13.5, -58.25) * mm, "end": v(-13.5, -58.25) * mm, "construction": true});
            skLineSegment(sketch, "E136.left", {"start": v(13.5, -31.25) * mm, "end": v(13.5, -58.25) * mm, "construction": true});
            skLineSegment(sketch, "E136.right", {"start": v(-13.5, -31.25) * mm, "end": v(-13.5, -55.5) * mm, "construction": true});
            skArc(sketch, "E137", {"start": v(-10, -52.25) * mm, "mid": v(-8.23, -52.98) * mm, "end": v(-7.5, -54.75) * mm});
            skArc(sketch, "E138", {"start": v(-10, -37.25) * mm, "mid": v(-8.23, -36.52) * mm, "end": v(-7.5, -34.75) * mm});
            skArc(sketch, "E139", {"start": v(7.5, -34.75) * mm, "mid": v(8.23, -36.52) * mm, "end": v(10, -37.25) * mm});
            skArc(sketch, "E140", {"start": v(10, -52.25) * mm, "mid": v(8.23, -52.98) * mm, "end": v(7.5, -54.75) * mm});
            skLineSegment(sketch, "E141.0", {"start": v(18.25, -22) * mm, "end": v(-18.25, -22) * mm, "construction": true});
            skLineSegment(sketch, "E141.1", {"start": v(18.25, -22) * mm, "end": v(18.25, -58.5) * mm, "construction": true});
            skLineSegment(sketch, "E141.2", {"start": v(18.25, -58.5) * mm, "end": v(-18.25, -58.5) * mm, "construction": true});
            skLineSegment(sketch, "E141.3", {"start": v(-18.25, -22) * mm, "end": v(-18.25, -58.5) * mm, "construction": true});
            skLineSegment(sketch, "E142", {"start": v(-7.5, -54.75) * mm, "end": v(-7.5, -58.5) * mm});
            skLineSegment(sketch, "E143", {"start": v(7.5, -54.75) * mm, "end": v(7.5, -58.5) * mm});
            skLineSegment(sketch, "E144", {"start": v(-7.5, -58.5) * mm, "end": v(7.5, -58.5) * mm});
            skLineSegment(sketch, "E145.0", {"start": v(-13.75, -31) * mm, "end": v(-13.75, -58.5) * mm, "construction": true});
            skLineSegment(sketch, "E145.1", {"start": v(13.75, -31) * mm, "end": v(-13.75, -31) * mm, "construction": true});
            skLineSegment(sketch, "E145.2", {"start": v(13.75, -31) * mm, "end": v(13.75, -58.5) * mm, "construction": true});
            skLineSegment(sketch, "E146", {"start": v(-7.5, -34.75) * mm, "end": v(-7.5, -31) * mm});
            skLineSegment(sketch, "E147", {"start": v(7.5, -34.75) * mm, "end": v(7.5, -31) * mm});
            skLineSegment(sketch, "E148", {"start": v(-18.25, -37.25) * mm, "end": v(-18.25, -52.5) * mm});
            skLineSegment(sketch, "E149", {"start": v(18.25, -37.25) * mm, "end": v(18.25, -52.5) * mm});
            skArc(sketch, "E150", {"start": v(-15.25, -28) * mm, "mid": v(-13.13, -27.12) * mm, "end": v(-12.25, -25) * mm});
            skArc(sketch, "E151", {"start": v(12.25, -25) * mm, "mid": v(13.13, -27.12) * mm, "end": v(15.25, -28) * mm});
            skLineSegment(sketch, "E152", {"start": v(-12.25, -25) * mm, "end": v(-12.25, -22) * mm});
            skLineSegment(sketch, "E153", {"start": v(-15.25, -28) * mm, "end": v(-18.25, -28) * mm});
            skLineSegment(sketch, "E154", {"start": v(-15.25, -31.75) * mm, "end": v(-18.25, -31.75) * mm});
            skLineSegment(sketch, "E155", {"start": v(-18.25, -28) * mm, "end": v(-18.25, -31.75) * mm});
            skLineSegment(sketch, "E156", {"start": v(15.25, -28) * mm, "end": v(18.25, -28) * mm});
            skLineSegment(sketch, "E157", {"start": v(12.25, -25) * mm, "end": v(12.25, -22) * mm});
            skLineSegment(sketch, "E158", {"start": v(-12.25, -22) * mm, "end": v(-2.5, -22) * mm});
            skLineSegment(sketch, "E159", {"start": v(-2.5, -22) * mm, "end": v(-2.5, -25) * mm});
            skLineSegment(sketch, "E160", {"start": v(-7.5, -31) * mm, "end": v(7.5, -31) * mm});
            skArc(sketch, "E161", {"start": v(-15.25, -31.75) * mm, "mid": v(-10.48, -29.77) * mm, "end": v(-8.5, -25) * mm});
            skLineSegment(sketch, "E162", {"start": v(-8.5, -25) * mm, "end": v(-2.5, -25) * mm});
            skLineSegment(sketch, "E163.MirrorCS", {"start": v(2.5, -22) * mm, "end": v(2.5, -25) * mm});
            skArc(sketch, "E164.MirrorCS", {"start": v(15.25, -31.75) * mm, "mid": v(10.48, -29.77) * mm, "end": v(8.5, -25) * mm});
            skLineSegment(sketch, "E165.MirrorCS", {"start": v(15.25, -31.75) * mm, "end": v(18.25, -31.75) * mm});
            skLineSegment(sketch, "E166", {"start": v(2.5, -25) * mm, "end": v(8.5, -25) * mm});
            skLineSegment(sketch, "E167", {"start": v(2.5, -22) * mm, "end": v(12.25, -22) * mm});
            skLineSegment(sketch, "E168", {"start": v(18.25, -31.75) * mm, "end": v(18.25, -28) * mm});
            skLineSegment(sketch, "E169", {"start": v(-18.25, -52.5) * mm, "end": v(-15.25, -52.5) * mm});
            skLineSegment(sketch, "E170", {"start": v(18.25, -52.5) * mm, "end": v(15.25, -52.5) * mm});
            skLineSegment(sketch, "E171", {"start": v(-10, -52.25) * mm, "end": v(-13.75, -52.25) * mm});
            skLineSegment(sketch, "E172", {"start": v(-13.75, -52.25) * mm, "end": v(-15.25, -52.5) * mm});
            skLineSegment(sketch, "E173", {"start": v(10, -52.25) * mm, "end": v(13.75, -52.25) * mm});
            skLineSegment(sketch, "E174", {"start": v(13.75, -52.25) * mm, "end": v(15.25, -52.5) * mm});
            skLineSegment(sketch, "E175", {"start": v(-10, -37.25) * mm, "end": v(-13.75, -37.25) * mm});
            skLineSegment(sketch, "E176", {"start": v(10, -37.25) * mm, "end": v(13.75, -37.25) * mm});
            skLineSegment(sketch, "E177", {"start": v(-13.75, -37.25) * mm, "end": v(-18.25, -37.25) * mm});
            skLineSegment(sketch, "E178", {"start": v(13.75, -37.25) * mm, "end": v(18.25, -37.25) * mm});
            skLineSegment(sketch, "E179", {"start": v(-15.25, 15.25) * mm, "end": v(15.25, -15.25) * mm, "construction": true});
            skLineSegment(sketch, "E180", {"start": v(15.25, 15.25) * mm, "end": v(-15.25, -15.25) * mm, "construction": true});
            skLineSegment(sketch, "E181", {"start": v(-14.66, 10.42) * mm, "end": v(-5.66, 1.41) * mm});
            skLineSegment(sketch, "E182", {"start": v(-5.66, -1.41) * mm, "end": v(-14.66, -10.42) * mm});
            skLineSegment(sketch, "E183", {"start": v(-7.6, 11.84) * mm, "end": v(-1.41, 5.66) * mm});
            skLineSegment(sketch, "E184", {"start": v(1.41, 5.66) * mm, "end": v(7.6, 11.84) * mm});
            skLineSegment(sketch, "E185", {"start": v(-6.18, 15.25) * mm, "end": v(6.18, 15.25) * mm});
            skLineSegment(sketch, "E186", {"start": v(-16.08, 11) * mm, "end": v(-18, 11) * mm});
            skLineSegment(sketch, "E187", {"start": v(-20, 9) * mm, "end": v(-20, -9) * mm});
            skLineSegment(sketch, "E188", {"start": v(-18, -11) * mm, "end": v(-16.08, -11) * mm});
            skLineSegment(sketch, "E189.MirrorCS", {"start": v(14.66, 10.42) * mm, "end": v(5.66, 1.41) * mm});
            skLineSegment(sketch, "E190.MirrorCS", {"start": v(5.66, -1.41) * mm, "end": v(14.66, -10.42) * mm});
            skLineSegment(sketch, "E191.MirrorCS", {"start": v(16.08, 11) * mm, "end": v(18, 11) * mm});
            skLineSegment(sketch, "E192.MirrorCS", {"start": v(18, -11) * mm, "end": v(16.08, -11) * mm});
            skLineSegment(sketch, "E193.MirrorCS", {"start": v(20, 9) * mm, "end": v(20, -9) * mm});
            skLineSegment(sketch, "E194.MirrorCS", {"start": v(1.41, -5.66) * mm, "end": v(7.6, -11.84) * mm});
            skLineSegment(sketch, "E195.MirrorCS", {"start": v(-7.6, -11.84) * mm, "end": v(-1.41, -5.66) * mm});
            skLineSegment(sketch, "E196.MirrorCS", {"start": v(-6.18, -15.25) * mm, "end": v(6.18, -15.25) * mm});
            skPoint(sketch, "E197.visualSharp", {"position": v(-11, 15.25) * mm});
            skArc(sketch, "E197.filletArc", {"start": v(-6.18, 15.25) * mm, "mid": v(-8.03, 14.02) * mm, "end": v(-7.6, 11.84) * mm});
            skPoint(sketch, "E198.visualSharp", {"position": v(11, 15.25) * mm});
            skArc(sketch, "E198.filletArc", {"start": v(7.6, 11.84) * mm, "mid": v(8.03, 14.02) * mm, "end": v(6.18, 15.25) * mm});
            skPoint(sketch, "E199.visualSharp", {"position": v(-20, 11) * mm});
            skArc(sketch, "E199.filletArc", {"start": v(-18, 11) * mm, "mid": v(-19.41, 10.42) * mm, "end": v(-20, 9) * mm});
            skPoint(sketch, "E200.visualSharp", {"position": v(-15.25, 11) * mm});
            skArc(sketch, "E200.filletArc", {"start": v(-14.66, 10.42) * mm, "mid": v(-15.31, 10.86) * mm, "end": v(-16.08, 11) * mm});
            skPoint(sketch, "E201.visualSharp", {"position": v(-20, -11) * mm});
            skArc(sketch, "E201.filletArc", {"start": v(-20, -9) * mm, "mid": v(-19.41, -10.42) * mm, "end": v(-18, -11) * mm});
            skPoint(sketch, "E202.visualSharp", {"position": v(-15.25, -11) * mm});
            skArc(sketch, "E202.filletArc", {"start": v(-16.08, -11) * mm, "mid": v(-15.31, -10.86) * mm, "end": v(-14.66, -10.42) * mm});
            skPoint(sketch, "E203.visualSharp", {"position": v(-4.24, 0) * mm});
            skArc(sketch, "E203.filletArc", {"start": v(-5.66, -1.41) * mm, "mid": v(-5.07, 0) * mm, "end": v(-5.66, 1.41) * mm});
            skPoint(sketch, "E204.visualSharp", {"position": v(0, 4.24) * mm});
            skArc(sketch, "E204.filletArc", {"start": v(-1.41, 5.66) * mm, "mid": v(0, 5.07) * mm, "end": v(1.41, 5.66) * mm});
            skPoint(sketch, "E205.visualSharp", {"position": v(-11, -15.25) * mm});
            skArc(sketch, "E205.filletArc", {"start": v(-7.6, -11.84) * mm, "mid": v(-8.03, -14.02) * mm, "end": v(-6.18, -15.25) * mm});
            skPoint(sketch, "E206.visualSharp", {"position": v(0, -4.24) * mm});
            skArc(sketch, "E206.filletArc", {"start": v(1.41, -5.66) * mm, "mid": v(0, -5.07) * mm, "end": v(-1.41, -5.66) * mm});
            skPoint(sketch, "E207.visualSharp", {"position": v(11, -15.25) * mm});
            skArc(sketch, "E207.filletArc", {"start": v(6.18, -15.25) * mm, "mid": v(8.03, -14.02) * mm, "end": v(7.6, -11.84) * mm});
            skPoint(sketch, "E208.visualSharp", {"position": v(4.24, 0) * mm});
            skArc(sketch, "E208.filletArc", {"start": v(5.66, 1.41) * mm, "mid": v(5.07, 0) * mm, "end": v(5.66, -1.41) * mm});
            skPoint(sketch, "E209.visualSharp", {"position": v(20, 11) * mm});
            skArc(sketch, "E209.filletArc", {"start": v(20, 9) * mm, "mid": v(19.41, 10.42) * mm, "end": v(18, 11) * mm});
            skPoint(sketch, "E210.visualSharp", {"position": v(15.25, 11) * mm});
            skArc(sketch, "E210.filletArc", {"start": v(16.08, 11) * mm, "mid": v(15.31, 10.86) * mm, "end": v(14.66, 10.42) * mm});
            skPoint(sketch, "E211.visualSharp", {"position": v(15.25, -11) * mm});
            skArc(sketch, "E211.filletArc", {"start": v(14.66, -10.42) * mm, "mid": v(15.31, -10.86) * mm, "end": v(16.08, -11) * mm});
            skPoint(sketch, "E212.visualSharp", {"position": v(20, -11) * mm});
            skArc(sketch, "E212.filletArc", {"start": v(18, -11) * mm, "mid": v(19.41, -10.42) * mm, "end": v(20, -9) * mm});
            skCircle(sketch, "E213", {"center": v(0, 0) * mm, "radius": 2.25 * mm});
            skSolve(sketch);
        }
        {
            var Q0;
            Q0=qSketchRegion(id+"F10",true);
            extrude(context, id + "F11", {"entities" : qUnion([Q0]), "operationType" : NewBodyOperationType.REMOVE, "endBound" : BoundingType.THROUGH_ALL, "oppositeDirection" : true, "depth" : 25 * mm, "offsetDistance" : 25 * mm});
        }
        {
            var Q0;
            Q0=makeQuery(id+"F11.boolean.opBoolean","COPY",EDGE,{"derivedFrom":makeQuery(id+"F11.opExtrude","SWEPT_EDGE",EDGE,{"disambiguationData":[OSD([sQuery(id+"F10.wireOp",EDGE,"E157"),sQuery(id+"F10.wireOp",EDGE,"E167")])]})});
            var Q1;
            Q1=makeQuery(id+"F11.boolean.opBoolean","COPY",EDGE,{"derivedFrom":makeQuery(id+"F11.opExtrude","SWEPT_EDGE",EDGE,{"disambiguationData":[OSD([sQuery(id+"F10.wireOp",EDGE,"E156"),sQuery(id+"F10.wireOp",EDGE,"E168")])]})});
            var Q2;
            Q2=makeQuery(id+"F11.boolean.opBoolean","COPY",EDGE,{"derivedFrom":makeQuery(id+"F11.opExtrude","SWEPT_EDGE",EDGE,{"disambiguationData":[OSD([sQuery(id+"F10.wireOp",EDGE,"E149"),sQuery(id+"F10.wireOp",EDGE,"E170")])]})});
            var Q3;
            Q3=makeQuery(id+"F11.boolean.opBoolean","COPY",EDGE,{"derivedFrom":makeQuery(id+"F11.opExtrude","SWEPT_EDGE",EDGE,{"disambiguationData":[OSD([sQuery(id+"F10.wireOp",EDGE,"E165.MirrorCS"),sQuery(id+"F10.wireOp",EDGE,"E168")])]})});
            var Q4;
            Q4=makeQuery(id+"F11.boolean.opBoolean","COPY",EDGE,{"derivedFrom":makeQuery(id+"F11.opExtrude","SWEPT_EDGE",EDGE,{"disambiguationData":[OSD([sQuery(id+"F10.wireOp",EDGE,"E149"),sQuery(id+"F10.wireOp",EDGE,"E178")])]})});
            var Q5;
            Q5=makeQuery(id+"F11.boolean.opBoolean","COPY",EDGE,{"derivedFrom":makeQuery(id+"F11.opExtrude","SWEPT_EDGE",EDGE,{"disambiguationData":[OSD([sQuery(id+"F10.wireOp",EDGE,"E147"),sQuery(id+"F10.wireOp",EDGE,"E160")])]})});
            var Q6;
            Q6=makeQuery(id+"F11.boolean.opBoolean","COPY",EDGE,{"derivedFrom":makeQuery(id+"F11.opExtrude","SWEPT_EDGE",EDGE,{"disambiguationData":[OSD([sQuery(id+"F10.wireOp",EDGE,"E143"),sQuery(id+"F10.wireOp",EDGE,"E144")])]})});
            var Q7;
            Q7=makeQuery(id+"F11.boolean.opBoolean","COPY",EDGE,{"derivedFrom":makeQuery(id+"F11.opExtrude","SWEPT_EDGE",EDGE,{"disambiguationData":[OSD([sQuery(id+"F10.wireOp",EDGE,"E163.MirrorCS"),sQuery(id+"F10.wireOp",EDGE,"E167")])]})});
            var Q8;
            Q8=makeQuery(id+"F11.boolean.opBoolean","COPY",EDGE,{"derivedFrom":makeQuery(id+"F11.opExtrude","SWEPT_EDGE",EDGE,{"disambiguationData":[OSD([sQuery(id+"F10.wireOp",EDGE,"E163.MirrorCS"),sQuery(id+"F10.wireOp",EDGE,"E166")])]})});
            var Q9;
            Q9=makeQuery(id+"F11.boolean.opBoolean","COPY",EDGE,{"derivedFrom":makeQuery(id+"F11.opExtrude","SWEPT_EDGE",EDGE,{"disambiguationData":[OSD([sQuery(id+"F10.wireOp",EDGE,"E164.MirrorCS"),sQuery(id+"F10.wireOp",EDGE,"E166")])]})});
            var Q10;
            Q10=makeQuery(id+"F11.boolean.opBoolean","COPY",EDGE,{"derivedFrom":makeQuery(id+"F11.opExtrude","SWEPT_EDGE",EDGE,{"disambiguationData":[OSD([sQuery(id+"F10.wireOp",EDGE,"E142"),sQuery(id+"F10.wireOp",EDGE,"E144")])]})});
            var Q11;
            Q11=makeQuery(id+"F11.boolean.opBoolean","COPY",EDGE,{"derivedFrom":makeQuery(id+"F11.opExtrude","SWEPT_EDGE",EDGE,{"disambiguationData":[OSD([sQuery(id+"F10.wireOp",EDGE,"E148"),sQuery(id+"F10.wireOp",EDGE,"E169")])]})});
            var Q12;
            Q12=makeQuery(id+"F11.boolean.opBoolean","COPY",EDGE,{"derivedFrom":makeQuery(id+"F11.opExtrude","SWEPT_EDGE",EDGE,{"disambiguationData":[OSD([sQuery(id+"F10.wireOp",EDGE,"E154"),sQuery(id+"F10.wireOp",EDGE,"E155")])]})});
            var Q13;
            Q13=makeQuery(id+"F11.boolean.opBoolean","COPY",EDGE,{"derivedFrom":makeQuery(id+"F11.opExtrude","SWEPT_EDGE",EDGE,{"disambiguationData":[OSD([sQuery(id+"F10.wireOp",EDGE,"E161"),sQuery(id+"F10.wireOp",EDGE,"E162")])]})});
            var Q14;
            Q14=makeQuery(id+"F11.boolean.opBoolean","COPY",EDGE,{"derivedFrom":makeQuery(id+"F11.opExtrude","SWEPT_EDGE",EDGE,{"disambiguationData":[OSD([sQuery(id+"F10.wireOp",EDGE,"E146"),sQuery(id+"F10.wireOp",EDGE,"E160")])]})});
            var Q15;
            Q15=makeQuery(id+"F11.boolean.opBoolean","COPY",EDGE,{"derivedFrom":makeQuery(id+"F11.opExtrude","SWEPT_EDGE",EDGE,{"disambiguationData":[OSD([sQuery(id+"F10.wireOp",EDGE,"E153"),sQuery(id+"F10.wireOp",EDGE,"E155")])]})});
            var Q16;
            Q16=makeQuery(id+"F11.boolean.opBoolean","COPY",EDGE,{"derivedFrom":makeQuery(id+"F11.opExtrude","SWEPT_EDGE",EDGE,{"disambiguationData":[OSD([sQuery(id+"F10.wireOp",EDGE,"E152"),sQuery(id+"F10.wireOp",EDGE,"E158")])]})});
            var Q17;
            Q17=makeQuery(id+"F11.boolean.opBoolean","COPY",EDGE,{"derivedFrom":makeQuery(id+"F11.opExtrude","SWEPT_EDGE",EDGE,{"disambiguationData":[OSD([sQuery(id+"F10.wireOp",EDGE,"E158"),sQuery(id+"F10.wireOp",EDGE,"E159")])]})});
            var Q18;
            Q18=makeQuery(id+"F11.boolean.opBoolean","COPY",EDGE,{"derivedFrom":makeQuery(id+"F11.opExtrude","SWEPT_EDGE",EDGE,{"disambiguationData":[OSD([sQuery(id+"F10.wireOp",EDGE,"E159"),sQuery(id+"F10.wireOp",EDGE,"E162")])]})});
            var Q19;
            Q19=makeQuery(id+"F11.boolean.opBoolean","COPY",EDGE,{"derivedFrom":makeQuery(id+"F11.opExtrude","SWEPT_EDGE",EDGE,{"disambiguationData":[OSD([sQuery(id+"F10.wireOp",EDGE,"E148"),sQuery(id+"F10.wireOp",EDGE,"E177")])]})});
            fillet(context, id + "F12", {"entities" : qUnion([Q0, Q1, Q2, Q3, Q4, Q5, Q6, Q7, Q8, Q9, Q10, Q11, Q12, Q13, Q14, Q15, Q16, Q17, Q18, Q19]), "radius" : 1 * mm, "allowEdgeOverflow" : false});
        }
        {
            var Q0;
            Q0=qCreatedBy(makeId("Top.planeOp"),FACE);
            var sketch = newSketch(context, id + "F13", { "sketchPlane" : qUnion([Q0])});
            skLineSegment(sketch, "E214.0.0", {"start": v(-20, 9) * mm, "end": v(-20, -9) * mm});
            skArc(sketch, "E214.0.1", {"start": v(-20, -9) * mm, "mid": v(-19.41, -10.42) * mm, "end": v(-18, -11) * mm});
            skLineSegment(sketch, "E214.0.2", {"start": v(-18, -11) * mm, "end": v(-16.08, -11) * mm});
            skArc(sketch, "E214.0.3", {"start": v(-16.08, -11) * mm, "mid": v(-15.31, -10.86) * mm, "end": v(-14.66, -10.42) * mm});
            skLineSegment(sketch, "E214.0.4", {"start": v(-14.66, -10.42) * mm, "end": v(-5.66, -1.41) * mm});
            skArc(sketch, "E214.0.5", {"start": v(-5.66, -1.41) * mm, "mid": v(-5.07, 0) * mm, "end": v(-5.66, 1.41) * mm});
            skLineSegment(sketch, "E214.0.6", {"start": v(-5.66, 1.41) * mm, "end": v(-14.66, 10.42) * mm});
            skArc(sketch, "E214.0.7", {"start": v(-14.66, 10.42) * mm, "mid": v(-15.31, 10.86) * mm, "end": v(-16.08, 11) * mm});
            skLineSegment(sketch, "E214.0.8", {"start": v(-16.08, 11) * mm, "end": v(-18, 11) * mm});
            skArc(sketch, "E214.0.9", {"start": v(-18, 11) * mm, "mid": v(-19.41, 10.42) * mm, "end": v(-20, 9) * mm});
            skLineSegment(sketch, "E215.0.0", {"start": v(1.41, 5.66) * mm, "end": v(7.6, 11.84) * mm});
            skArc(sketch, "E215.0.1", {"start": v(7.6, 11.84) * mm, "mid": v(8.03, 14.02) * mm, "end": v(6.18, 15.25) * mm});
            skLineSegment(sketch, "E215.0.2", {"start": v(6.18, 15.25) * mm, "end": v(-6.18, 15.25) * mm});
            skArc(sketch, "E215.0.3", {"start": v(-6.18, 15.25) * mm, "mid": v(-8.03, 14.02) * mm, "end": v(-7.6, 11.84) * mm});
            skLineSegment(sketch, "E215.0.4", {"start": v(-7.6, 11.84) * mm, "end": v(-1.41, 5.66) * mm});
            skArc(sketch, "E215.0.5", {"start": v(-1.41, 5.66) * mm, "mid": v(0, 5.07) * mm, "end": v(1.41, 5.66) * mm});
            skLineSegment(sketch, "E216.0.0", {"start": v(-1.41, -5.66) * mm, "end": v(-7.6, -11.84) * mm});
            skArc(sketch, "E216.0.1", {"start": v(-7.6, -11.84) * mm, "mid": v(-8.03, -14.02) * mm, "end": v(-6.18, -15.25) * mm});
            skLineSegment(sketch, "E216.0.2", {"start": v(-6.18, -15.25) * mm, "end": v(6.18, -15.25) * mm});
            skArc(sketch, "E216.0.3", {"start": v(6.18, -15.25) * mm, "mid": v(8.03, -14.02) * mm, "end": v(7.6, -11.84) * mm});
            skLineSegment(sketch, "E216.0.4", {"start": v(7.6, -11.84) * mm, "end": v(1.41, -5.66) * mm});
            skArc(sketch, "E216.0.5", {"start": v(1.41, -5.66) * mm, "mid": v(0, -5.07) * mm, "end": v(-1.41, -5.66) * mm});
            skLineSegment(sketch, "E217.0.0", {"start": v(16.08, -11) * mm, "end": v(18, -11) * mm});
            skArc(sketch, "E217.0.1", {"start": v(18, -11) * mm, "mid": v(19.41, -10.42) * mm, "end": v(20, -9) * mm});
            skLineSegment(sketch, "E217.0.2", {"start": v(20, -9) * mm, "end": v(20, 9) * mm});
            skArc(sketch, "E217.0.3", {"start": v(20, 9) * mm, "mid": v(19.41, 10.42) * mm, "end": v(18, 11) * mm});
            skLineSegment(sketch, "E217.0.4", {"start": v(18, 11) * mm, "end": v(16.08, 11) * mm});
            skArc(sketch, "E217.0.5", {"start": v(16.08, 11) * mm, "mid": v(15.31, 10.86) * mm, "end": v(14.66, 10.42) * mm});
            skLineSegment(sketch, "E217.0.6", {"start": v(14.66, 10.42) * mm, "end": v(5.66, 1.41) * mm});
            skArc(sketch, "E217.0.7", {"start": v(5.66, 1.41) * mm, "mid": v(5.07, 0) * mm, "end": v(5.66, -1.41) * mm});
            skLineSegment(sketch, "E217.0.8", {"start": v(5.66, -1.41) * mm, "end": v(14.66, -10.42) * mm});
            skArc(sketch, "E217.0.9", {"start": v(14.66, -10.42) * mm, "mid": v(15.31, -10.86) * mm, "end": v(16.08, -11) * mm});
            skCircle(sketch, "E218", {"center": v(0, 0) * mm, "radius": 1.5 * mm});
            skSolve(sketch);
        }
        {
            var Q0;
            Q0=qSketchRegion(id+"F13",true);
            extrude(context, id + "F14", {"entities" : qUnion([Q0]), "operationType" : NewBodyOperationType.REMOVE, "endBound" : BoundingType.THROUGH_ALL, "depth" : 25 * mm, "offsetDistance" : 25 * mm});
        }
        {
            var Q0;
            Q0=qSketchRegion(id+"F13",true);
            extrude(context, id + "F15", {"entities" : qUnion([Q0]), "operationType" : NewBodyOperationType.REMOVE, "endBound" : BoundingType.THROUGH_ALL, "depth" : 25 * mm, "offsetDistance" : 25 * mm});
        }
        {
            var Q0;
            Q0=qCreatedBy(makeId("Top.planeOp"),FACE);
            var sketch = newSketch(context, id + "F16", { "sketchPlane" : qUnion([Q0])});
            skLineSegment(sketch, "E219", {"start": v(-17.54, 20.84) * mm, "end": v(-4, 20.84) * mm, "construction": true});
            skLineSegment(sketch, "E220.MirrorCS", {"start": v(17.54, 20.84) * mm, "end": v(4, 20.84) * mm, "construction": true});
            skLineSegment(sketch, "E221.MirrorCS", {"start": v(-17.54, -20.84) * mm, "end": v(-4, -20.84) * mm, "construction": true});
            skLineSegment(sketch, "E222.MirrorCS", {"start": v(17.54, -20.84) * mm, "end": v(4, -20.84) * mm, "construction": true});
            skArc(sketch, "E223.0.startCap", {"start": v(-17.54, 19.6) * mm, "mid": v(-18.8, 20.84) * mm, "end": v(-17.54, 22.1) * mm});
            skArc(sketch, "E223.0.endCap", {"start": v(-4, 22.1) * mm, "mid": v(-2.75, 20.84) * mm, "end": v(-4, 19.6) * mm});
            skLineSegment(sketch, "E223.0.left", {"start": v(-17.54, 22.1) * mm, "end": v(-4, 22.1) * mm});
            skLineSegment(sketch, "E223.0.right", {"start": v(-17.54, 19.6) * mm, "end": v(-4, 19.6) * mm});
            skArc(sketch, "E224.0.startCap", {"start": v(17.54, 22.1) * mm, "mid": v(18.8, 20.84) * mm, "end": v(17.54, 19.6) * mm});
            skArc(sketch, "E224.0.endCap", {"start": v(4, 19.6) * mm, "mid": v(2.75, 20.84) * mm, "end": v(4, 22.1) * mm});
            skLineSegment(sketch, "E224.0.left", {"start": v(17.54, 19.6) * mm, "end": v(4, 19.6) * mm});
            skLineSegment(sketch, "E224.0.right", {"start": v(17.54, 22.1) * mm, "end": v(4, 22.1) * mm});
            skArc(sketch, "E225.0.startCap", {"start": v(-17.54, -22.1) * mm, "mid": v(-18.8, -20.84) * mm, "end": v(-17.54, -19.6) * mm});
            skArc(sketch, "E225.0.endCap", {"start": v(-4, -19.6) * mm, "mid": v(-2.75, -20.84) * mm, "end": v(-4, -22.1) * mm});
            skLineSegment(sketch, "E225.0.left", {"start": v(-17.54, -19.6) * mm, "end": v(-4, -19.6) * mm});
            skLineSegment(sketch, "E225.0.right", {"start": v(-17.54, -22.1) * mm, "end": v(-4, -22.1) * mm});
            skArc(sketch, "E226.0.startCap", {"start": v(17.54, -19.6) * mm, "mid": v(18.8, -20.84) * mm, "end": v(17.54, -22.1) * mm});
            skArc(sketch, "E226.0.endCap", {"start": v(4, -22.1) * mm, "mid": v(2.75, -20.84) * mm, "end": v(4, -19.6) * mm});
            skLineSegment(sketch, "E226.0.left", {"start": v(17.54, -22.1) * mm, "end": v(4, -22.1) * mm});
            skLineSegment(sketch, "E226.0.right", {"start": v(17.54, -19.6) * mm, "end": v(4, -19.6) * mm});
            skSolve(sketch);
        }
        {
            var Q0;
            Q0=qSketchRegion(id+"F16",true);
            extrude(context, id + "F17", {"entities" : qUnion([Q0]), "operationType" : NewBodyOperationType.REMOVE, "endBound" : BoundingType.THROUGH_ALL, "depth" : 25 * mm, "offsetDistance" : 25 * mm});
        }
        {
            var Q0;
            Q0=qCreatedBy(makeId("Top.planeOp"),FACE);
            var sketch = newSketch(context, id + "F18", { "sketchPlane" : qUnion([Q0])});
            skLineSegment(sketch, "E227.bottom", {"start": v(22.5, 39.35) * mm, "end": v(-22.5, 39.35) * mm, "construction": true});
            skLineSegment(sketch, "E227.top", {"start": v(22.5, 18.5) * mm, "end": v(-22.5, 18.5) * mm, "construction": true});
            skLineSegment(sketch, "E227.left", {"start": v(22.5, 39.35) * mm, "end": v(22.5, 18.5) * mm, "construction": true});
            skLineSegment(sketch, "E227.right", {"start": v(-22.5, 39.35) * mm, "end": v(-22.5, 18.5) * mm, "construction": true});
            skPoint(sketch, "E227.middle", {"position": v(0, 28.92) * mm});
            skLineSegment(sketch, "E228", {"start": v(-22.5, 39.35) * mm, "end": v(0, 28.92) * mm, "construction": true});
            skLineSegment(sketch, "E229", {"start": v(22.5, 39.35) * mm, "end": v(0, 28.92) * mm, "construction": true});
            skLineSegment(sketch, "E230", {"start": v(0, 28.92) * mm, "end": v(22.5, 18.5) * mm, "construction": true});
            skLineSegment(sketch, "E231", {"start": v(0, 28.92) * mm, "end": v(-22.5, 18.5) * mm, "construction": true});
            skLineSegment(sketch, "E232.0", {"start": v(-21, 32.3) * mm, "end": v(-21, 25.54) * mm});
            skLineSegment(sketch, "E232.1", {"start": v(-16.74, 35.03) * mm, "end": v(-7.48, 30.74) * mm});
            skLineSegment(sketch, "E232.2", {"start": v(-7.48, 27.1) * mm, "end": v(-16.74, 22.82) * mm});
            skLineSegment(sketch, "E233.0", {"start": v(8.9, 38.35) * mm, "end": v(-8.9, 38.35) * mm});
            skLineSegment(sketch, "E233.1", {"start": v(9.73, 34.53) * mm, "end": v(1.26, 30.6) * mm});
            skLineSegment(sketch, "E233.2", {"start": v(-9.73, 34.53) * mm, "end": v(-1.26, 30.6) * mm});
            skLineSegment(sketch, "E234.0", {"start": v(8.9, 19.5) * mm, "end": v(-8.9, 19.5) * mm});
            skLineSegment(sketch, "E234.1", {"start": v(1.26, 27.23) * mm, "end": v(9.73, 23.3) * mm});
            skLineSegment(sketch, "E234.2", {"start": v(-1.26, 27.23) * mm, "end": v(-9.73, 23.3) * mm});
            skLineSegment(sketch, "E235.0", {"start": v(21, 32.3) * mm, "end": v(21, 25.54) * mm});
            skLineSegment(sketch, "E235.1", {"start": v(16.74, 35.03) * mm, "end": v(7.48, 30.74) * mm});
            skLineSegment(sketch, "E235.2", {"start": v(7.48, 27.1) * mm, "end": v(16.74, 22.82) * mm});
            skPoint(sketch, "E236.visualSharp", {"position": v(-21, 37) * mm});
            skArc(sketch, "E236.filletArc", {"start": v(-16.74, 35.03) * mm, "mid": v(-19.61, 34.83) * mm, "end": v(-21, 32.3) * mm});
            skPoint(sketch, "E237.visualSharp", {"position": v(-21, 20.84) * mm});
            skArc(sketch, "E237.filletArc", {"start": v(-21, 25.54) * mm, "mid": v(-19.61, 23.01) * mm, "end": v(-16.74, 22.82) * mm});
            skPoint(sketch, "E238.visualSharp", {"position": v(-3.57, 28.92) * mm});
            skArc(sketch, "E238.filletArc", {"start": v(-7.48, 27.1) * mm, "mid": v(-6.32, 28.92) * mm, "end": v(-7.48, 30.74) * mm});
            skPoint(sketch, "E239.visualSharp", {"position": v(-17.96, 19.5) * mm});
            skArc(sketch, "E239.filletArc", {"start": v(-9.73, 23.3) * mm, "mid": v(-10.84, 21.06) * mm, "end": v(-8.9, 19.5) * mm});
            skPoint(sketch, "E240.visualSharp", {"position": v(17.96, 19.5) * mm});
            skArc(sketch, "E240.filletArc", {"start": v(8.9, 19.5) * mm, "mid": v(10.84, 21.06) * mm, "end": v(9.73, 23.3) * mm});
            skPoint(sketch, "E241.visualSharp", {"position": v(-17.96, 38.35) * mm});
            skArc(sketch, "E241.filletArc", {"start": v(-8.9, 38.35) * mm, "mid": v(-10.84, 36.78) * mm, "end": v(-9.73, 34.53) * mm});
            skPoint(sketch, "E242.visualSharp", {"position": v(17.96, 38.35) * mm});
            skArc(sketch, "E242.filletArc", {"start": v(9.73, 34.53) * mm, "mid": v(10.84, 36.78) * mm, "end": v(8.9, 38.35) * mm});
            skPoint(sketch, "E243.visualSharp", {"position": v(0, 30.02) * mm});
            skArc(sketch, "E243.filletArc", {"start": v(-1.26, 30.6) * mm, "mid": v(0, 30.33) * mm, "end": v(1.26, 30.6) * mm});
            skPoint(sketch, "E244.visualSharp", {"position": v(0, 27.82) * mm});
            skArc(sketch, "E244.filletArc", {"start": v(1.26, 27.23) * mm, "mid": v(0, 27.51) * mm, "end": v(-1.26, 27.23) * mm});
            skPoint(sketch, "E245.visualSharp", {"position": v(3.57, 28.92) * mm});
            skArc(sketch, "E245.filletArc", {"start": v(7.48, 30.74) * mm, "mid": v(6.32, 28.92) * mm, "end": v(7.48, 27.1) * mm});
            skPoint(sketch, "E246.visualSharp", {"position": v(21, 37) * mm});
            skArc(sketch, "E246.filletArc", {"start": v(21, 32.3) * mm, "mid": v(19.61, 34.83) * mm, "end": v(16.74, 35.03) * mm});
            skPoint(sketch, "E247.visualSharp", {"position": v(21, 20.84) * mm});
            skArc(sketch, "E247.filletArc", {"start": v(16.74, 22.82) * mm, "mid": v(19.61, 23.01) * mm, "end": v(21, 25.54) * mm});
            skLineSegment(sketch, "E248.MirrorCS", {"start": v(-21, -32.3) * mm, "end": v(-21, -25.54) * mm});
            skArc(sketch, "E249.MirrorCS", {"start": v(-16.74, -35.03) * mm, "mid": v(-19.61, -34.83) * mm, "end": v(-21, -32.3) * mm});
            skLineSegment(sketch, "E250.MirrorCS", {"start": v(-16.74, -35.03) * mm, "end": v(-7.48, -30.74) * mm});
            skArc(sketch, "E251.MirrorCS", {"start": v(-7.48, -27.1) * mm, "mid": v(-6.32, -28.92) * mm, "end": v(-7.48, -30.74) * mm});
            skLineSegment(sketch, "E252.MirrorCS", {"start": v(-7.48, -27.1) * mm, "end": v(-16.74, -22.82) * mm});
            skArc(sketch, "E253.MirrorCS", {"start": v(-9.73, -23.3) * mm, "mid": v(-10.84, -21.06) * mm, "end": v(-8.9, -19.5) * mm});
            skLineSegment(sketch, "E254.MirrorCS", {"start": v(-1.26, -27.23) * mm, "end": v(-9.73, -23.3) * mm});
            skLineSegment(sketch, "E255.MirrorCS", {"start": v(1.26, -27.23) * mm, "end": v(9.73, -23.3) * mm});
            skLineSegment(sketch, "E256.MirrorCS", {"start": v(8.9, -19.5) * mm, "end": v(-8.9, -19.5) * mm});
            skArc(sketch, "E257.MirrorCS", {"start": v(8.9, -19.5) * mm, "mid": v(10.84, -21.06) * mm, "end": v(9.73, -23.3) * mm});
            skArc(sketch, "E258.MirrorCS", {"start": v(1.26, -27.23) * mm, "mid": v(0, -27.51) * mm, "end": v(-1.26, -27.23) * mm});
            skArc(sketch, "E259.MirrorCS", {"start": v(-1.26, -30.6) * mm, "mid": v(0, -30.33) * mm, "end": v(1.26, -30.6) * mm});
            skLineSegment(sketch, "E260.MirrorCS", {"start": v(-9.73, -34.53) * mm, "end": v(-1.26, -30.6) * mm});
            skLineSegment(sketch, "E261.MirrorCS", {"start": v(9.73, -34.53) * mm, "end": v(1.26, -30.6) * mm});
            skArc(sketch, "E262.MirrorCS", {"start": v(-8.9, -38.35) * mm, "mid": v(-10.84, -36.78) * mm, "end": v(-9.73, -34.53) * mm});
            skArc(sketch, "E263.MirrorCS", {"start": v(9.73, -34.53) * mm, "mid": v(10.84, -36.78) * mm, "end": v(8.9, -38.35) * mm});
            skLineSegment(sketch, "E264.MirrorCS", {"start": v(8.9, -38.35) * mm, "end": v(-8.9, -38.35) * mm});
            skArc(sketch, "E265.MirrorCS", {"start": v(7.48, -30.74) * mm, "mid": v(6.32, -28.92) * mm, "end": v(7.48, -27.1) * mm});
            skLineSegment(sketch, "E266.MirrorCS", {"start": v(16.74, -35.03) * mm, "end": v(7.48, -30.74) * mm});
            skArc(sketch, "E267.MirrorCS", {"start": v(21, -32.3) * mm, "mid": v(19.61, -34.83) * mm, "end": v(16.74, -35.03) * mm});
            skLineSegment(sketch, "E268.MirrorCS", {"start": v(21, -32.3) * mm, "end": v(21, -25.54) * mm});
            skArc(sketch, "E269.MirrorCS", {"start": v(16.74, -22.82) * mm, "mid": v(19.61, -23.01) * mm, "end": v(21, -25.54) * mm});
            skLineSegment(sketch, "E270.MirrorCS", {"start": v(7.48, -27.1) * mm, "end": v(16.74, -22.82) * mm});
            skArc(sketch, "E271.MirrorCS", {"start": v(-21, -25.54) * mm, "mid": v(-19.61, -23.01) * mm, "end": v(-16.74, -22.82) * mm});
            skSolve(sketch);
        }
        {
            var Q0;
            Q0=qSketchRegion(id+"F18",true);
            extrude(context, id + "F19", {"entities" : qUnion([Q0]), "operationType" : NewBodyOperationType.REMOVE, "endBound" : BoundingType.THROUGH_ALL, "depth" : 25 * mm, "offsetDistance" : 25 * mm});
        }
        {
            var Q0;
            Q0=makeQuery(id+"F3.opExtrude","CAP_FACE",FACE,{"disambiguationData":[OSD([sQuery(id+"F2.wireOp",EDGE,"E36.0"),sQuery(id+"F2.wireOp",EDGE,"E37.0"),sQuery(id+"F2.wireOp",EDGE,"E38.0"),sQuery(id+"F2.wireOp",EDGE,"E39.0"),sQuery(id+"F2.wireOp",EDGE,"E40.0"),sQuery(id+"F2.wireOp",EDGE,"E41.0"),sQuery(id+"F2.wireOp",EDGE,"E42.0"),sQuery(id+"F2.wireOp",EDGE,"E43.0"),sQuery(id+"F2.wireOp",EDGE,"E44.0"),sQuery(id+"F2.wireOp",EDGE,"E45.0"),sQuery(id+"F2.wireOp",EDGE,"E46.0"),sQuery(id+"F2.wireOp",EDGE,"E47.bottom"),sQuery(id+"F2.wireOp",EDGE,"E47.top"),sQuery(id+"F2.wireOp",EDGE,"E47.left"),sQuery(id+"F2.wireOp",EDGE,"E47.right"),sQuery(id+"F2.wireOp",EDGE,"E48"),sQuery(id+"F2.wireOp",EDGE,"E49"),sQuery(id+"F2.wireOp",EDGE,"E50"),sQuery(id+"F2.wireOp",EDGE,"E51.MirrorCS"),sQuery(id+"F2.wireOp",EDGE,"E52.MirrorCS"),sQuery(id+"F2.wireOp",EDGE,"E53.MirrorCS"),sQuery(id+"F2.wireOp",EDGE,"E54"),sQuery(id+"F2.wireOp",EDGE,"E55.MirrorCS"),sQuery(id+"F2.wireOp",EDGE,"E57"),sQuery(id+"F2.wireOp",EDGE,"E63"),sQuery(id+"F2.wireOp",EDGE,"E65"),sQuery(id+"F2.wireOp",EDGE,"E67"),sQuery(id+"F2.wireOp",EDGE,"E69"),sQuery(id+"F2.wireOp",EDGE,"E72"),sQuery(id+"F2.wireOp",EDGE,"E75"),sQuery(id+"F2.wireOp",EDGE,"E78"),sQuery(id+"F2.wireOp",EDGE,"E79"),sQuery(id+"F2.wireOp",EDGE,"E80")])],"isStart":false});
            var sketch = newSketch(context, id + "F20", { "sketchPlane" : qUnion([Q0])});
            skLineSegment(sketch, "E272.bottom", {"start": v(14.5, 67) * mm, "end": v(-14.5, 67) * mm, "construction": true});
            skLineSegment(sketch, "E272.top", {"start": v(14.5, 17) * mm, "end": v(-14.5, 17) * mm, "construction": true});
            skLineSegment(sketch, "E272.left", {"start": v(14.5, 67) * mm, "end": v(14.5, 17) * mm, "construction": true});
            skLineSegment(sketch, "E272.right", {"start": v(-14.5, 67) * mm, "end": v(-14.5, 17) * mm, "construction": true});
            skPoint(sketch, "E272.middle", {"position": v(0, 42) * mm});
            skLineSegment(sketch, "E273.bottom", {"start": v(5, 37) * mm, "end": v(-5, 37) * mm, "construction": true});
            skLineSegment(sketch, "E273.top", {"start": v(5, 47) * mm, "end": v(-5, 47) * mm, "construction": true});
            skLineSegment(sketch, "E273.left", {"start": v(5, 37) * mm, "end": v(5, 47) * mm, "construction": true});
            skLineSegment(sketch, "E273.right", {"start": v(-5, 37) * mm, "end": v(-5, 47) * mm, "construction": true});
            skLineSegment(sketch, "E274", {"start": v(-5, 47) * mm, "end": v(-5, 57) * mm, "construction": true});
            skLineSegment(sketch, "E275", {"start": v(-5, 37) * mm, "end": v(-5, 27) * mm, "construction": true});
            skLineSegment(sketch, "E276", {"start": v(-5, 27) * mm, "end": v(5, 27) * mm, "construction": true});
            skLineSegment(sketch, "E277", {"start": v(5, 27) * mm, "end": v(5, 37) * mm, "construction": true});
            skLineSegment(sketch, "E278", {"start": v(-5, 57) * mm, "end": v(5, 57) * mm, "construction": true});
            skLineSegment(sketch, "E279", {"start": v(5, 57) * mm, "end": v(5, 47) * mm, "construction": true});
            skCircle(sketch, "E280", {"center": v(5, 47) * mm, "radius": 1 * mm});
            skCircle(sketch, "E281", {"center": v(-5, 47) * mm, "radius": 1 * mm});
            skCircle(sketch, "E282", {"center": v(5, 37) * mm, "radius": 1 * mm});
            skCircle(sketch, "E283", {"center": v(-5, 37) * mm, "radius": 1 * mm});
            skCircle(sketch, "E284", {"center": v(-5, 27) * mm, "radius": 1 * mm});
            skCircle(sketch, "E285", {"center": v(5, 27) * mm, "radius": 1 * mm});
            skCircle(sketch, "E286", {"center": v(20, 58) * mm, "radius": 1.25 * mm});
            skCircle(sketch, "E287", {"center": v(20, 45) * mm, "radius": 1.25 * mm});
            skCircle(sketch, "E288.MirrorC", {"center": v(-20, 58) * mm, "radius": 1.25 * mm});
            skCircle(sketch, "E289.MirrorC", {"center": v(-20, 45) * mm, "radius": 1.25 * mm});
            skLineSegment(sketch, "E290", {"start": v(9, 58) * mm, "end": v(9, 51.5) * mm, "construction": true});
            skLineSegment(sketch, "E291", {"start": v(9, 51.5) * mm, "end": v(0, 51.5) * mm, "construction": true});
            skLineSegment(sketch, "E292.MirrorCS", {"start": v(-9, 58) * mm, "end": v(-9, 51.5) * mm, "construction": true});
            skLineSegment(sketch, "E293.MirrorCS", {"start": v(-9, 51.5) * mm, "end": v(0, 51.5) * mm, "construction": true});
            skLineSegment(sketch, "E294.0", {"start": v(23, 62) * mm, "end": v(-23, 62) * mm, "construction": true});
            skArc(sketch, "E295.0.startCap", {"start": v(8, 58) * mm, "mid": v(9, 59) * mm, "end": v(10, 58) * mm});
            skArc(sketch, "E295.0.endCap", {"start": v(10, 51.5) * mm, "mid": v(9.7, 50.8) * mm, "end": v(9, 50.5) * mm});
            skLineSegment(sketch, "E295.0.left", {"start": v(10, 58) * mm, "end": v(10, 51.5) * mm});
            skLineSegment(sketch, "E295.0.right", {"start": v(8, 58) * mm, "end": v(8, 53.5) * mm});
            skArc(sketch, "E295.1.startCap", {"start": v(10, 51.5) * mm, "mid": v(9.7, 50.8) * mm, "end": v(9, 50.5) * mm});
            skLineSegment(sketch, "E295.1.left", {"start": v(9, 50.5) * mm, "end": v(2.25, 50.5) * mm});
            skLineSegment(sketch, "E295.1.right", {"start": v(7, 52.5) * mm, "end": v(2.25, 52.5) * mm});
            skArc(sketch, "E295.2.startCap", {"start": v(-9, 50.5) * mm, "mid": v(-9.7, 50.8) * mm, "end": v(-10, 51.5) * mm});
            skLineSegment(sketch, "E295.2.left", {"start": v(-7, 52.5) * mm, "end": v(-2.25, 52.5) * mm});
            skLineSegment(sketch, "E295.2.right", {"start": v(-9, 50.5) * mm, "end": v(-2.25, 50.5) * mm});
            skArc(sketch, "E295.3.startCap", {"start": v(-10, 58) * mm, "mid": v(-9, 59) * mm, "end": v(-8, 58) * mm});
            skArc(sketch, "E295.3.endCap", {"start": v(-9, 50.5) * mm, "mid": v(-9.7, 50.8) * mm, "end": v(-10, 51.5) * mm});
            skLineSegment(sketch, "E295.3.left", {"start": v(-8, 58) * mm, "end": v(-8, 53.5) * mm});
            skLineSegment(sketch, "E295.3.right", {"start": v(-10, 58) * mm, "end": v(-10, 51.5) * mm});
            skPoint(sketch, "E296.visualSharp", {"position": v(-8, 52.5) * mm});
            skArc(sketch, "E296.filletArc", {"start": v(-8, 53.5) * mm, "mid": v(-7.7, 52.8) * mm, "end": v(-7, 52.5) * mm});
            skPoint(sketch, "E297.visualSharp", {"position": v(8, 52.5) * mm});
            skArc(sketch, "E297.filletArc", {"start": v(7, 52.5) * mm, "mid": v(7.7, 52.8) * mm, "end": v(8, 53.5) * mm});
            skArc(sketch, "E298", {"start": v(-5, 44.5) * mm, "mid": v(-3.23, 45.23) * mm, "end": v(-2.5, 47) * mm});
            skArc(sketch, "E299", {"start": v(2.5, 47) * mm, "mid": v(3.23, 45.23) * mm, "end": v(5, 44.5) * mm});
            skArc(sketch, "E300", {"start": v(-5, 29.5) * mm, "mid": v(-3.23, 28.77) * mm, "end": v(-2.5, 27) * mm});
            skArc(sketch, "E301", {"start": v(5, 29.5) * mm, "mid": v(3.23, 28.77) * mm, "end": v(2.5, 27) * mm});
            skLineSegment(sketch, "E302", {"start": v(-2.5, 47) * mm, "end": v(-2.5, 48) * mm});
            skLineSegment(sketch, "E303", {"start": v(-2.5, 48) * mm, "end": v(2.5, 48) * mm});
            skLineSegment(sketch, "E304", {"start": v(2.5, 48) * mm, "end": v(2.5, 47) * mm});
            skLineSegment(sketch, "E305", {"start": v(-2.5, 27) * mm, "end": v(-2.5, 26) * mm});
            skLineSegment(sketch, "E306", {"start": v(-2.5, 26) * mm, "end": v(2.5, 26) * mm});
            skLineSegment(sketch, "E307", {"start": v(2.5, 26) * mm, "end": v(2.5, 27) * mm});
            skArc(sketch, "E308", {"start": v(-5, 39.5) * mm, "mid": v(-2.5, 37) * mm, "end": v(-5, 34.5) * mm});
            skArc(sketch, "E309", {"start": v(5, 39.5) * mm, "mid": v(2.5, 37) * mm, "end": v(5, 34.5) * mm});
            skLineSegment(sketch, "E310", {"start": v(-5, 44.5) * mm, "end": v(-6, 44.5) * mm});
            skLineSegment(sketch, "E311", {"start": v(-6, 44.5) * mm, "end": v(-6, 39.5) * mm});
            skLineSegment(sketch, "E312", {"start": v(-6, 39.5) * mm, "end": v(-5, 39.5) * mm});
            skLineSegment(sketch, "E313", {"start": v(5, 44.5) * mm, "end": v(6, 44.5) * mm});
            skLineSegment(sketch, "E314", {"start": v(6, 44.5) * mm, "end": v(6, 39.5) * mm});
            skLineSegment(sketch, "E315", {"start": v(6, 39.5) * mm, "end": v(5, 39.5) * mm});
            skLineSegment(sketch, "E316", {"start": v(-5, 34.5) * mm, "end": v(-6, 34.5) * mm});
            skLineSegment(sketch, "E317", {"start": v(-6, 34.5) * mm, "end": v(-6, 29.5) * mm});
            skLineSegment(sketch, "E318", {"start": v(-6, 29.5) * mm, "end": v(-5, 29.5) * mm});
            skLineSegment(sketch, "E319", {"start": v(5, 34.5) * mm, "end": v(6, 34.5) * mm});
            skLineSegment(sketch, "E320", {"start": v(6, 34.5) * mm, "end": v(6, 29.5) * mm});
            skLineSegment(sketch, "E321", {"start": v(6, 29.5) * mm, "end": v(5, 29.5) * mm});
            skArc(sketch, "E322", {"start": v(-2.25, 52.5) * mm, "mid": v(-1.25, 51.5) * mm, "end": v(-2.25, 50.5) * mm});
            skArc(sketch, "E323.MirrorCS", {"start": v(2.25, 52.5) * mm, "mid": v(1.25, 51.5) * mm, "end": v(2.25, 50.5) * mm});
            skPoint(sketch, "E324.orphan", {"position": v(0, 52.5) * mm});
            skPoint(sketch, "E325.orphan", {"position": v(0, 50.5) * mm});
            skLineSegment(sketch, "E326", {"start": v(-14.5, 32.61) * mm, "end": v(-14.5, 25.61) * mm, "construction": true});
            skArc(sketch, "E327.0.startCap", {"start": v(-16, 32.61) * mm, "mid": v(-14.5, 34.11) * mm, "end": v(-13, 32.61) * mm});
            skArc(sketch, "E327.0.endCap", {"start": v(-13, 25.61) * mm, "mid": v(-14.5, 24.11) * mm, "end": v(-16, 25.61) * mm});
            skLineSegment(sketch, "E327.0.left", {"start": v(-13, 32.61) * mm, "end": v(-13, 25.61) * mm});
            skLineSegment(sketch, "E327.0.right", {"start": v(-16, 32.61) * mm, "end": v(-16, 25.61) * mm});
            skArc(sketch, "E328.MirrorCS", {"start": v(13, 25.61) * mm, "mid": v(14.5, 24.11) * mm, "end": v(16, 25.61) * mm});
            skArc(sketch, "E329.MirrorCS", {"start": v(16, 32.61) * mm, "mid": v(14.5, 34.11) * mm, "end": v(13, 32.61) * mm});
            skLineSegment(sketch, "E330.MirrorCS", {"start": v(16, 32.61) * mm, "end": v(16, 25.61) * mm});
            skLineSegment(sketch, "E331.MirrorCS", {"start": v(13, 32.61) * mm, "end": v(13, 25.61) * mm});
            skPoint(sketch, "E332", {"position": v(-25, 29.11) * mm});
            skPoint(sketch, "E333", {"position": v(-14.5, 29.11) * mm});
            skPoint(sketch, "E334", {"position": v(-25, 37) * mm});
            skPoint(sketch, "E335", {"position": v(25, 37) * mm});
            skLineSegment(sketch, "E336", {"start": v(-25, 37) * mm, "end": v(25, 37) * mm, "construction": true});
            skArc(sketch, "E337.MirrorCS", {"start": v(-13, 48.39) * mm, "mid": v(-14.5, 49.89) * mm, "end": v(-16, 48.39) * mm});
            skArc(sketch, "E338.MirrorCS", {"start": v(-16, 41.39) * mm, "mid": v(-14.5, 39.89) * mm, "end": v(-13, 41.39) * mm});
            skLineSegment(sketch, "E339.MirrorCS", {"start": v(-16, 41.39) * mm, "end": v(-16, 48.39) * mm});
            skLineSegment(sketch, "E340.MirrorCS", {"start": v(-13, 41.39) * mm, "end": v(-13, 48.39) * mm});
            skArc(sketch, "E341.MirrorCS", {"start": v(16, 41.39) * mm, "mid": v(14.5, 39.89) * mm, "end": v(13, 41.39) * mm});
            skArc(sketch, "E342.MirrorCS", {"start": v(13, 48.39) * mm, "mid": v(14.5, 49.89) * mm, "end": v(16, 48.39) * mm});
            skLineSegment(sketch, "E343.MirrorCS", {"start": v(13, 41.39) * mm, "end": v(13, 48.39) * mm});
            skLineSegment(sketch, "E344.MirrorCS", {"start": v(16, 41.39) * mm, "end": v(16, 48.39) * mm});
            skSolve(sketch);
        }
        {
            var Q0;
            Q0=qSketchRegion(id+"F20",true);
            extrude(context, id + "F21", {"entities" : qUnion([Q0]), "operationType" : NewBodyOperationType.REMOVE, "endBound" : BoundingType.THROUGH_ALL, "oppositeDirection" : true, "depth" : 25 * mm, "offsetDistance" : 25 * mm});
        }
        {
            var Q0;
            Q0=makeQuery(id+"F21.boolean.opBoolean","COPY",EDGE,{"derivedFrom":makeQuery(id+"F21.opExtrude","SWEPT_EDGE",EDGE,{"disambiguationData":[OSD([sQuery(id+"F20.wireOp",EDGE,"E310"),sQuery(id+"F20.wireOp",EDGE,"E311")])]})});
            var Q1;
            Q1=makeQuery(id+"F21.boolean.opBoolean","COPY",EDGE,{"derivedFrom":makeQuery(id+"F21.opExtrude","SWEPT_EDGE",EDGE,{"disambiguationData":[OSD([sQuery(id+"F20.wireOp",EDGE,"E302"),sQuery(id+"F20.wireOp",EDGE,"E303")])]})});
            var Q2;
            Q2=makeQuery(id+"F21.boolean.opBoolean","COPY",EDGE,{"derivedFrom":makeQuery(id+"F21.opExtrude","SWEPT_EDGE",EDGE,{"disambiguationData":[OSD([sQuery(id+"F20.wireOp",EDGE,"E303"),sQuery(id+"F20.wireOp",EDGE,"E304")])]})});
            var Q3;
            Q3=makeQuery(id+"F21.boolean.opBoolean","COPY",EDGE,{"derivedFrom":makeQuery(id+"F21.opExtrude","SWEPT_EDGE",EDGE,{"disambiguationData":[OSD([sQuery(id+"F20.wireOp",EDGE,"E313"),sQuery(id+"F20.wireOp",EDGE,"E314")])]})});
            var Q4;
            Q4=makeQuery(id+"F21.boolean.opBoolean","COPY",EDGE,{"derivedFrom":makeQuery(id+"F21.opExtrude","SWEPT_EDGE",EDGE,{"disambiguationData":[OSD([sQuery(id+"F20.wireOp",EDGE,"E319"),sQuery(id+"F20.wireOp",EDGE,"E320")])]})});
            var Q5;
            Q5=makeQuery(id+"F21.boolean.opBoolean","COPY",EDGE,{"derivedFrom":makeQuery(id+"F21.opExtrude","SWEPT_EDGE",EDGE,{"disambiguationData":[OSD([sQuery(id+"F20.wireOp",EDGE,"E316"),sQuery(id+"F20.wireOp",EDGE,"E317")])]})});
            var Q6;
            Q6=makeQuery(id+"F21.boolean.opBoolean","COPY",EDGE,{"derivedFrom":makeQuery(id+"F21.opExtrude","SWEPT_EDGE",EDGE,{"disambiguationData":[OSD([sQuery(id+"F20.wireOp",EDGE,"E305"),sQuery(id+"F20.wireOp",EDGE,"E306")])]})});
            var Q7;
            Q7=makeQuery(id+"F21.boolean.opBoolean","COPY",EDGE,{"derivedFrom":makeQuery(id+"F21.opExtrude","SWEPT_EDGE",EDGE,{"disambiguationData":[OSD([sQuery(id+"F20.wireOp",EDGE,"E317"),sQuery(id+"F20.wireOp",EDGE,"E318")])]})});
            var Q8;
            Q8=makeQuery(id+"F21.boolean.opBoolean","COPY",EDGE,{"derivedFrom":makeQuery(id+"F21.opExtrude","SWEPT_EDGE",EDGE,{"disambiguationData":[OSD([sQuery(id+"F20.wireOp",EDGE,"E311"),sQuery(id+"F20.wireOp",EDGE,"E312")])]})});
            var Q9;
            Q9=makeQuery(id+"F21.boolean.opBoolean","COPY",EDGE,{"derivedFrom":makeQuery(id+"F21.opExtrude","SWEPT_EDGE",EDGE,{"disambiguationData":[OSD([sQuery(id+"F20.wireOp",EDGE,"E314"),sQuery(id+"F20.wireOp",EDGE,"E315")])]})});
            var Q10;
            Q10=makeQuery(id+"F21.boolean.opBoolean","COPY",EDGE,{"derivedFrom":makeQuery(id+"F21.opExtrude","SWEPT_EDGE",EDGE,{"disambiguationData":[OSD([sQuery(id+"F20.wireOp",EDGE,"E320"),sQuery(id+"F20.wireOp",EDGE,"E321")])]})});
            var Q11;
            Q11=makeQuery(id+"F21.boolean.opBoolean","COPY",EDGE,{"derivedFrom":makeQuery(id+"F21.opExtrude","SWEPT_EDGE",EDGE,{"disambiguationData":[OSD([sQuery(id+"F20.wireOp",EDGE,"E306"),sQuery(id+"F20.wireOp",EDGE,"E307")])]})});
            fillet(context, id + "F22", {"entities" : qUnion([Q0, Q1, Q2, Q3, Q4, Q5, Q6, Q7, Q8, Q9, Q10, Q11]), "radius" : 1 * mm, "allowEdgeOverflow" : false});
        }
    });
